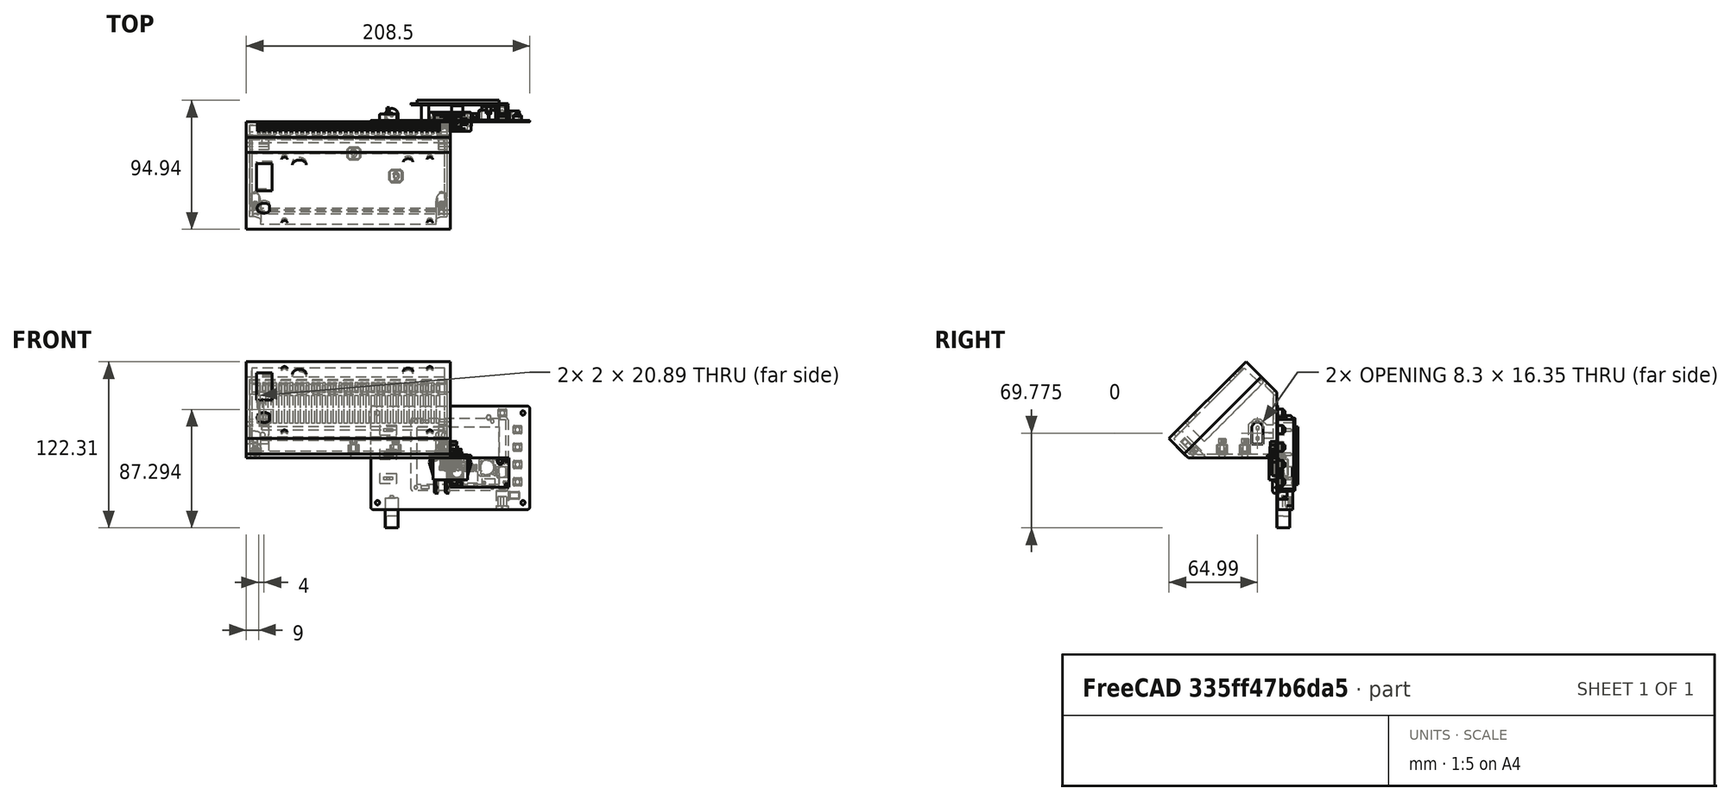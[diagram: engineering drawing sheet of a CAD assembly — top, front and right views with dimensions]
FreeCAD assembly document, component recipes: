
FREECAD ASSEMBLY — COMPONENT RECIPES ("oscillo_010_surBase35mm_007.5")

This assembly document has 19 components, labeled P0..P18 below (a component is one placed body or linked part). 12 of them carry a construction recipe — the FreeCAD feature program that regenerates the part from scratch, quoted from this document or its linked companion documents; the rest are supplied as boundary geometry only. No exploded tour is included for this assembly.
COMPONENT P0 — recipe-attached ("base", modeled in this document).
Construction recipe (the document's own serialized feature program — sketch geometry with constraints, then the solid features built on it; lengths are millimeters unless a unit is written):

FEATURE [PartDesign::FeatureBase] Clone
  BaseFeature = -> Slice_child0
FEATURE [PartDesign::Thickness] Thickness
  Base = -> Clone [Face7]
  BaseFeature = -> Clone
  Intersection = false
  Join = 0
  Mode = 0
  Reversed = true
  SupportTransform = false
  Value = 2.5
  expr: Value = <<sp>>.epaisseurParois
FEATURE [PartDesign::Plane] DatumPlane001  label="planXt"
  AttachmentOffset = pos=(0,0,-2.5) rot=(0,0,1;0rad)
  Length = 110.737
  MapMode = 5
  Placement = pos=(-2.5,6e-16,-6e-16) rot=(0.57735,0.57735,0.57735;2.0944rad)
  ResizeMode = 0
  Support = -> [YZ_Plane002]
  Width = 102.305
  expr: .AttachmentOffset.Base.z = -<<sp>>.epaisseurParois
FEATURE [Sketcher::SketchObject] Sketch002  label="sk_renfortXt"
  FullyConstrained = true
  MapMode = 5
  Placement = pos=(-2.5,6e-16,-6e-16) rot=(0.57735,0.57735,0.57735;2.0944rad)
  Support = -> [DatumPlane001]
  expr: .Constraints.dist = <<sp>>.xt60distanceAngleBord
  expr: .Constraints.epRf = <<sp>>.xt60epRenfort
  expr: Constraints[13] = <<sp>>.xt60largeurFetiere
  expr: Constraints[14] = <<sp>>.xt60hauteur
  expr: Constraints[15] = <<sp>>.xt60hauteurToit
  expr: Constraints[16] = <<sp>>.xt60base
  expr: Constraints[18] = .Constraints.dist
  expr: Constraints[31] = <<sp>>.epaisseurParois
  expr: Constraints[32] = .Constraints.epRf
  expr: Constraints[34] = .Constraints.epRf
  expr: Constraints[45] = <<sp>>.epaisseurParois
  sketch-geometry (17):
    g0: LineSegment StartX=-18.3 StartY=10 StartZ=0 EndX=-18.3 EndY=23.25 EndZ=0
    g1: LineSegment StartX=-18.3 StartY=23.25 StartZ=0 EndX=-15.65 EndY=25.75 EndZ=0
    g2: LineSegment StartX=-15.65 StartY=25.75 StartZ=0 EndX=-12.65 EndY=25.75 EndZ=0
    g3: LineSegment StartX=-12.65 StartY=25.75 StartZ=0 EndX=-10 EndY=23.25 EndZ=0
    g4: LineSegment StartX=-10 StartY=23.25 StartZ=0 EndX=-10 EndY=10 EndZ=0
    g5: LineSegment StartX=-10 StartY=10 StartZ=0 EndX=-18.3 EndY=10 EndZ=0
    g6: LineSegment StartX=-14.15 StartY=10 StartZ=0 EndX=-14.15 EndY=25.75 EndZ=0
    g7: LineSegment StartX=-16.6431 StartY=28.25 StartZ=0 EndX=-20.8 EndY=24.3284 EndZ=0
    g8: LineSegment StartX=-20.8 StartY=24.3284 StartZ=0 EndX=-20.8 EndY=2.5 EndZ=0
    g9: LineSegment StartX=-20.8 StartY=2.5 StartZ=0 EndX=-7.5 EndY=2.5 EndZ=0
    g10: LineSegment StartX=-7.5 StartY=2.5 StartZ=0 EndX=-7.5 EndY=24.3284 EndZ=0
    g11: LineSegment StartX=-7.5 StartY=24.3284 StartZ=0 EndX=-11.6569 EndY=28.25 EndZ=0
    g12: LineSegment StartX=-11.6569 StartY=28.25 StartZ=0 EndX=-16.6431 EndY=28.25 EndZ=0
    g13: LineSegment StartX=-7.5 StartY=24.3284 StartZ=0 EndX=-2.5 EndY=24.3284 EndZ=0
    g14: LineSegment StartX=-2.5 StartY=24.3284 StartZ=0 EndX=-2.5 EndY=2.5 EndZ=0
    g15: LineSegment StartX=-2.5 StartY=2.5 StartZ=0 EndX=-7.5 EndY=2.5 EndZ=0
    g16: LineSegment StartX=-7.5 StartY=2.5 StartZ=0 EndX=-7.5 EndY=24.3284 EndZ=0
  constraints (46):
    c: Vertical(g0)
    c: Coincident(g0,g1)
    c: Coincident(g1,g2)
    c: Horizontal(g2)
    c: Coincident(g2,g3)
    c: Coincident(g3,g4)
    c: Vertical(g4)
    c: Coincident(g4,g5)
    c: Coincident(g5,g0)
    c: Horizontal(g5)
    c: Symmetric(g1,g2,g6)
    c: Equal(g0,g4)
    c: Symmetric(g0,g4,g6)
    c: DistanceX(g2,g2) = 3
    c: DistanceY(g4,g4) = 13.25
    c: DistanceY(g3,g2) = 2.5
    c: DistanceX(g5,g5) = 8.3
    c: DistanceX(g4,g-1) = 10  'dist'
    c: DistanceY(g-1,g4) = 10
    c: Coincident(g7,g8)
    c: Vertical(g8)
    c: Coincident(g8,g9)
    c: Horizontal(g9)
    c: Coincident(g9,g10)
    c: Coincident(g10,g11)
    c: Coincident(g11,g12)
    c: Coincident(g12,g7)
    c: Symmetric(g7,g10,g6)
    c: Symmetric(g7,g11,g6)
    c: Symmetric(g8,g9,g6)
    c: DistanceX(g8,g0) = 2.5  'epRf'
    c: DistanceY(g-1,g9) = 2.5
    c: Distance(g7,g1) = 2.5
    c: Parallel(g1,g7)
    c: DistanceY(g2,g11) = 2.5
    c: Coincident(g13,g14)
    c: Coincident(g14,g15)
    c: Coincident(g15,g16)
    c: Coincident(g16,g13)
    c: Horizontal(g13)
    c: Horizontal(g15)
    c: Vertical(g14)
    c: Vertical(g16)
    c: Coincident(g13,g11)
    c: Horizontal(g14,g9)
    c: DistanceX(g14,g-1) = 2.5
FEATURE [PartDesign::Pad] Pad001  label="renfortXt"
  AllowMultiFace = false
  BaseFeature = -> Thickness
  Direction = (1,1,1)
  Length = 145
  Length2 = 100
  Profile = -> Sketch002
  Reversed = true
  Type = 0
  expr: Length = <<sp>>.largeurModuleBase - 2 * <<sp>>.epaisseurParois
FEATURE [Sketcher::SketchObject] Sketch003  label="sk_trouXt"
  FullyConstrained = true
  MapMode = 5
  Placement = pos=(0,0,0) rot=(0.57735,0.57735,0.57735;2.0944rad)
  Support = -> [YZ_Plane002]
  expr: .Constraints.dist = <<sp>>.xt60distanceAngleBord
  expr: Constraints[13] = <<sp>>.xt60base
  expr: Constraints[14] = <<sp>>.xt60hauteur
  expr: Constraints[15] = <<sp>>.xt60hauteurToit + <<sp>>.xtJeu
  expr: Constraints[16] = <<sp>>.xt60largeurFetiere
  expr: Constraints[18] = .Constraints.dist
  sketch-geometry (7):
    g0: LineSegment StartX=-18.3 StartY=10 StartZ=0 EndX=-18.3 EndY=23.25 EndZ=0
    g1: LineSegment StartX=-18.3 StartY=23.25 StartZ=0 EndX=-15.65 EndY=26.35 EndZ=0
    g2: LineSegment StartX=-15.65 StartY=26.35 StartZ=0 EndX=-12.65 EndY=26.35 EndZ=0
    g3: LineSegment StartX=-12.65 StartY=26.35 StartZ=0 EndX=-10 EndY=23.25 EndZ=0
    g4: LineSegment StartX=-10 StartY=23.25 StartZ=0 EndX=-10 EndY=10 EndZ=0
    g5: LineSegment StartX=-10 StartY=10 StartZ=0 EndX=-18.3 EndY=10 EndZ=0
    g6: LineSegment StartX=-14.15 StartY=10 StartZ=0 EndX=-14.15 EndY=26.35 EndZ=0
  constraints (19):
    c: Vertical(g0)
    c: Coincident(g0,g1)
    c: Coincident(g1,g2)
    c: Horizontal(g2)
    c: Coincident(g2,g3)
    c: Coincident(g3,g4)
    c: Coincident(g4,g5)
    c: Coincident(g5,g0)
    c: Horizontal(g5)
    c: Symmetric(g1,g2,g6)
    c: Symmetric(g0,g3,g6)
    c: Vertical(g6)
    c: Symmetric(g0,g4,g6)
    c: DistanceX(g5,g5) = 8.3
    c: DistanceY(g4,g4) = 13.25
    c: DistanceY(g3,g2) = 3.1
    c: DistanceX(g2,g2) = 3
    c: DistanceX(g4,g-1) = 10  'dist'
    c: DistanceY(g-1,g4) = 10
FEATURE [PartDesign::Pocket] Pocket
  AllowMultiFace = false
  BaseFeature = -> Pad001
  Direction = (1,1,1)
  Length = 150
  Length2 = 100
  Profile = -> Sketch003
  Type = 0
  expr: Length = <<sp>>.largeurModuleBase
FEATURE [PartDesign::Plane] DatumPlane002  label="planDecoupeRenfortXt"
  AttachmentOffset = pos=(0,0,2.5) rot=(0,0,1;0rad)
  Length = 199.331
  MapMode = 5
  Placement = pos=(0,-2.5,-6e-16) rot=(1,0,0;1.5708rad)
  ResizeMode = 0
  Support = -> [XZ_Plane002]
  Width = 108.899
  expr: .AttachmentOffset.Base.z = <<sp>>.epaisseurParois
FEATURE [Sketcher::SketchObject] Sketch004  label="sk_decoupRenfXt"
  FullyConstrained = true
  MapMode = 5
  Placement = pos=(0,-2.5,-6e-16) rot=(1,0,0;1.5708rad)
  Support = -> [DatumPlane002]
  expr: Constraints[10] = <<sp>>.xt60LongueurRenfortPetit + <<sp>>.epaisseurParois
  expr: Constraints[11] = <<sp>>.largeurModuleBase - (<<sp>>.xt60longueurRenfortGrand + <<sp>>.epaisseurParois)
  expr: Constraints[8] = <<sp>>.epaisseurParois
  expr: Constraints[9] = <<sp>>.xt60distanceAngleBord + <<sp>>.xt60hauteur + <<sp>>.xt60hauteurToit + <<sp>>.xt60epRenfort
  sketch-geometry (4):
    g0: LineSegment StartX=-133.5 StartY=28.25 StartZ=0 EndX=-8.5 EndY=28.25 EndZ=0
    g1: LineSegment StartX=-8.5 StartY=28.25 StartZ=0 EndX=-8.5 EndY=2.5 EndZ=0
    g2: LineSegment StartX=-8.5 StartY=2.5 StartZ=0 EndX=-133.5 EndY=2.5 EndZ=0
    g3: LineSegment StartX=-133.5 StartY=2.5 StartZ=0 EndX=-133.5 EndY=28.25 EndZ=0
  constraints (12):
    c: Coincident(g0,g1)
    c: Coincident(g1,g2)
    c: Coincident(g2,g3)
    c: Coincident(g3,g0)
    c: Horizontal(g0)
    c: Horizontal(g2)
    c: Vertical(g1)
    c: Vertical(g3)
    c: DistanceY(g-1,g1) = 2.5
    c: DistanceY(g-1,g0) = 28.25
    c: DistanceX(g1,g-1) = 8.5
    c: DistanceX(g2,g-1) = 133.5
FEATURE [PartDesign::Pocket] Pocket001  label="decoupeRenfXt"
  AllowMultiFace = false
  BaseFeature = -> Pocket
  Direction = (1,1,1)
  Length = 23.3
  Length2 = 100
  Profile = -> Sketch004
  Reversed = true
  Type = 0
  expr: Length = <<sp>>.xt60distanceAngleBord + <<sp>>.xt60base + 2 * <<sp>>.xt60epRenfort
FEATURE [Sketcher::SketchObject] Sketch005  label="xt60PercagePostMale"
  FullyConstrained = true
  MapMode = 5
  Placement = pos=(0,0,0) rot=(1,0,0;1.5708rad)
  Support = -> [XZ_Plane002]
  expr: Constraints[0] = <<sp>>.insertDiamPercage
  expr: Constraints[1] = <<sp>>.insertDistanceTrouBordMale
  expr: Constraints[2] = <<sp>>.insertHauteur
  sketch-geometry (1):
    g0: Circle CenterX=-4.5 CenterY=16.625 CenterZ=0 NormalX=0 NormalY=0 NormalZ=1 AngleXU=0 Radius=2
  constraints (3):
    c: Diameter(g0) = 4
    c: DistanceX(g0,g-1) = 4.5
    c: DistanceY(g-1,g0) = 16.625
FEATURE [PartDesign::Pocket] Pocket002  label="insertXtMale"
  AllowMultiFace = false
  BaseFeature = -> Pocket001
  Direction = (1,1,1)
  Length = 10
  Length2 = 100
  Profile = -> Sketch005
  Reversed = true
  Type = 0
  expr: Length = <<sp>>.insertProfondeurPercage
FEATURE [Sketcher::SketchObject] Sketch006  label="xt60PercagePostFem"
  FullyConstrained = true
  MapMode = 5
  Placement = pos=(0,0,0) rot=(1,0,0;1.5708rad)
  Support = -> [XZ_Plane002]
  expr: Constraints[0] = <<sp>>.insertDiamPercage
  expr: Constraints[1] = <<sp>>.insertDistanceTrouBordFem
  expr: Constraints[2] = <<sp>>.insertHauteur
  sketch-geometry (1):
    g0: Circle CenterX=-138 CenterY=16.625 CenterZ=0 NormalX=0 NormalY=0 NormalZ=1 AngleXU=0 Radius=2
  constraints (3):
    c: Diameter(g0) = 4
    c: DistanceX(g0,g-1) = 138
    c: DistanceY(g-1,g0) = 16.625
FEATURE [PartDesign::Pocket] Pocket003  label="insertXt60Fem"
  AllowMultiFace = false
  BaseFeature = -> Pocket002
  Direction = (1,1,1)
  Length = 10
  Length2 = 100
  Profile = -> Sketch006
  Reversed = true
  Type = 0
  expr: Length = <<sp>>.insertProfondeurPercage
FEATURE [PartDesign::Plane] DatumPlane003
  AttachmentOffset = pos=(0,0,2.5) rot=(0,0,1;0rad)
  Length = 200.515
  MapMode = 2
  Placement = pos=(0,0,2.5) rot=(0,0,1;0rad)
  ResizeMode = 0
  Support = -> [XY_Plane002]
  Width = 118.515
  expr: .AttachmentOffset.Base.z = <<sp>>.epaisseurParois
FEATURE [PartDesign::Plane] DatumPlane004  label="planTrancheur"
  AttachmentOffset = pos=(0,0,71) rot=(-1,0,0;0.785398rad)
  Length = 204.647
  MapMode = 5
  Placement = pos=(0,-71,-1.58e-14) rot=(1,0,0;0.785398rad)
  ResizeMode = 0
  Support = -> [XZ_Plane002]
  Width = 155.206
  expr: .AttachmentOffset.Base.z = <<sp>>.planTrancheur
FEATURE [Sketcher::SketchObject] Sketch008
  FullyConstrained = true
  MapMode = 5
  Placement = pos=(0,-71,-2.13e-14) rot=(1,0,0;0.785398rad)
  Support = -> [DatumPlane004]
  expr: .Constraints.dist = <<sp>>.epaisseurParois
  expr: Constraints[13] = <<sp>>.epaisseurParois
  expr: Constraints[16] = <<sp>>.insertDiamPercage / 2 + <<sp>>.insertFAVMargeDist
  expr: Constraints[1] = <<sp>>.insertFavDistAuZeroDuPLan
  expr: Constraints[21] = <<sp>>.insertFAVDistBord
  expr: Constraints[22] = <<sp>>.largeurModuleBase - <<sp>>.epaisseurParois
  sketch-geometry (7):
    g0: LineSegment StartX=-2.5 StartY=4.24264 StartZ=0 EndX=-147.5 EndY=4.24264 EndZ=0
    g1: LineSegment StartX=-6.5 StartY=14.7426 StartZ=0 EndX=-2.5 EndY=14.7426 EndZ=0
    g2: LineSegment StartX=-2.5 StartY=14.7426 StartZ=0 EndX=-2.5 EndY=6.74264 EndZ=0
    g3: LineSegment StartX=-2.5 StartY=6.74264 StartZ=0 EndX=-10.5 EndY=6.74264 EndZ=0
    g4: LineSegment StartX=-10.5 StartY=6.74264 StartZ=0 EndX=-10.5 EndY=10.7426 EndZ=0
    g5: ArcOfCircle CenterX=-6.5 CenterY=10.7426 CenterZ=0 NormalX=0 NormalY=0 NormalZ=1 AngleXU=0 Radius=4 StartAngle=1.5708 EndAngle=3.14159
    g6: LineSegment StartX=-6.5 StartY=10.7426 StartZ=0 EndX=-6.5 EndY=6.74264 EndZ=0
  constraints (23):
    c: Horizontal(g0)
    c: DistanceY(g-1,g0) = 4.24264
    c: DistanceX(g0,g-1) = 2.5  'dist'
    c: Horizontal(g1)
    c: Coincident(g1,g2)
    c: Vertical(g2)
    c: Coincident(g2,g3)
    c: Horizontal(g3)
    c: Coincident(g3,g4)
    c: Vertical(g4)
    c: Vertical(g2,g0)
    c: Equal(g3,g2)
    c: Equal(g4,g1)
    c: DistanceY(g0,g2) = 2.5
    c: Coincident(g5,g4)
    c: Coincident(g5,g1)
    c: DistanceX(g5,g2) = 4
    c: Coincident(g6,g5)
    c: PointOnObject(g6,g3)
    c: Vertical(g6)
    c: Vertical(g5,g1)
    c: DistanceX(g3,g3) = 8
    c: DistanceX(g0,g-1) = 147.5
FEATURE [PartDesign::Pad] Pad003  label="padTrouFAVDroite"
  AllowMultiFace = false
  BaseFeature = -> Pocket003
  Direction = (1,1,1)
  Length = 10
  Length2 = 100
  Profile = -> Sketch008
  Reversed = true
  Type = 3
  UpToFace = -> DatumPlane003
FEATURE [Sketcher::SketchObject] Sketch009
  FullyConstrained = true
  MapMode = 5
  Placement = pos=(0,-71,-2.13e-14) rot=(1,0,0;0.785398rad)
  Support = -> [DatumPlane004]
  expr: .Constraints.larg = <<sp>>.insertFAVDistBord
  expr: Constraints[11] = .Constraints.larg / 2
  expr: Constraints[12] = <<sp>>.largeurModuleBase
  expr: Constraints[13] = <<sp>>.insertFavDistAuZeroDuPLan
  expr: Constraints[14] = <<sp>>.epaisseurParois
  expr: Constraints[15] = <<sp>>.epaisseurParois
  expr: Constraints[8] = .Constraints.larg
  sketch-geometry (6):
    g0: LineSegment StartX=-147.5 StartY=6.74264 StartZ=0 EndX=-139.5 EndY=6.74264 EndZ=0
    g1: LineSegment StartX=-139.5 StartY=6.74264 StartZ=0 EndX=-139.5 EndY=10.7426 EndZ=0
    g2: LineSegment StartX=-143.5 StartY=14.7426 StartZ=0 EndX=-147.5 EndY=14.7426 EndZ=0
    g3: LineSegment StartX=-147.5 StartY=14.7426 StartZ=0 EndX=-147.5 EndY=6.74264 EndZ=0
    g4: ArcOfCircle CenterX=-143.5 CenterY=10.7426 CenterZ=0 NormalX=0 NormalY=0 NormalZ=1 AngleXU=0 Radius=4 StartAngle=0 EndAngle=1.5708
    g5: GeomPoint X=-150 Y=4.24264 Z=0
  constraints (16):
    c: Coincident(g0,g1)
    c: Coincident(g2,g3)
    c: Coincident(g3,g0)
    c: Horizontal(g0)
    c: Horizontal(g2)
    c: Vertical(g1)
    c: Vertical(g3)
    c: DistanceX(g0,g0) = 8  'larg'
    c: DistanceY(g3,g3) = 8
    c: Tangent(g2,g4) = -1.5708
    c: Tangent(g1,g4) = -1.5708
    c: DistanceX(g0,g4) = 4
    c: DistanceX(g5,g-1) = 150
    c: DistanceY(g-1,g5) = 4.24264
    c: DistanceX(g5,g0) = 2.5
    c: DistanceY(g5,g0) = 2.5
FEATURE [PartDesign::Pad] Pad004  label="padTrouFavGauche"
  AllowMultiFace = false
  BaseFeature = -> Pad003
  Direction = (1,1,1)
  Length = 10
  Length2 = 100
  Profile = -> Sketch009
  Type = 3
  UpToFace = -> DatumPlane003 [Plane]
FEATURE [Sketcher::SketchObject] Sketch010
  FullyConstrained = true
  MapMode = 5
  Placement = pos=(0,-71,-2.13e-14) rot=(1,0,0;0.785398rad)
  Support = -> [DatumPlane004]
  expr: Constraints[0] = <<sp>>.insertFAVDistBord / 2 + <<sp>>.epaisseurParois
  expr: Constraints[1] = <<sp>>.insertFavDistAuZeroDuPLan + <<sp>>.epaisseurParois + <<sp>>.insertFAVDistBord / 2
  expr: Constraints[2] = <<sp>>.insertDiamPercage
  sketch-geometry (1):
    g0: Circle CenterX=-6.5 CenterY=10.7426 CenterZ=0 NormalX=0 NormalY=0 NormalZ=1 AngleXU=0 Radius=2
  constraints (3):
    c: DistanceX(g0,g-1) = 6.5
    c: DistanceY(g-1,g0) = 10.7426
    c: Diameter(g0) = 4
FEATURE [PartDesign::Pocket] Pocket004  label="trouDroit"
  AllowMultiFace = false
  BaseFeature = -> Pad004
  Direction = (1,1,1)
  Length = 5
  Length2 = 100
  Profile = -> Sketch010
  Type = 1
FEATURE [Sketcher::SketchObject] Sketch011
  FullyConstrained = true
  MapMode = 5
  Placement = pos=(0,-71,-2.13e-14) rot=(1,0,0;0.785398rad)
  Support = -> [DatumPlane004]
  expr: Constraints[0] = <<sp>>.insertDiamPercage
  expr: Constraints[1] = <<sp>>.largeurModuleBase - <<sp>>.epaisseurParois - <<sp>>.insertFAVDistBord / 2
  expr: Constraints[2] = <<sp>>.insertFavDistAuZeroDuPLan + <<sp>>.epaisseurParois + <<sp>>.insertFAVDistBord / 2
  sketch-geometry (1):
    g0: Circle CenterX=-143.5 CenterY=10.7426 CenterZ=0 NormalX=0 NormalY=0 NormalZ=1 AngleXU=0 Radius=2
  constraints (3):
    c: Diameter(g0) = 4
    c: DistanceX(g0,g-1) = 143.5
    c: DistanceY(g-1,g0) = 10.7426
FEATURE [PartDesign::Pocket] Pocket005  label="trouGauche"
  AllowMultiFace = false
  BaseFeature = -> Pocket004
  Direction = (1,1,1)
  Length = 5
  Length2 = 100
  Profile = -> Sketch011
  Type = 1
FEATURE [PartDesign::Plane] DatumPlane005  label="planTeteVisFav"
  AttachmentOffset = pos=(0,0,68) rot=(-1,0,0;0.785398rad)
  Length = 204.647
  MapMode = 5
  Placement = pos=(0,-68,-1.51e-14) rot=(1,0,0;0.785398rad)
  ResizeMode = 0
  Support = -> [XZ_Plane002]
  Width = 155.206
  expr: .AttachmentOffset.Base.z = <<sp>>.planTrancheur - 3
FEATURE [Sketcher::SketchObject] Sketch012
  ExternalGeometry = -> [Pocket005]
  FullyConstrained = true
  MapMode = 5
  Placement = pos=(0,-68,-1.42e-14) rot=(1,0,0;0.785398rad)
  Support = -> [DatumPlane005]
  expr: Constraints[1] = <<sp>>.visM3DiamEncastrement
  sketch-geometry (2):
    g0: Circle CenterX=-6.5 CenterY=8.62132 CenterZ=0 NormalX=0 NormalY=0 NormalZ=1 AngleXU=0 Radius=3
    g1: Circle CenterX=-143.5 CenterY=8.62132 CenterZ=0 NormalX=0 NormalY=0 NormalZ=1 AngleXU=0 Radius=3
  constraints (4):
    c: Equal(g0,g1)
    c: Diameter(g1) = 6
    c: Coincident(g1,g-4)
    c: Coincident(g-3,g0)
FEATURE [PartDesign::Pocket] Pocket006  label="evidementTeteVisFav"
  AllowMultiFace = false
  BaseFeature = -> Pocket005
  Direction = (1,1,1)
  Length = 20
  Length2 = 100
  Profile = -> Sketch012
  Type = 1
FEATURE [Sketcher::SketchObject] Sketch014
  FullyConstrained = true
  MapMode = 5
  Placement = pos=(0,0,0) rot=(1,0,0;1.5708rad)
  Support = -> [XZ_Plane002]
  expr: Constraints[12] = <<sp>>.xt60distanceAngleBord + <<sp>>.xt60hauteur + <<sp>>.ventilDistBordFente
  expr: Constraints[13] = <<sp>>.ventilLargeurFentes
  expr: Constraints[14] = <<sp>>.ventilEcartfente / 2
  expr: Constraints[15] = <<sp>>.hauteurDuDos - <<sp>>.ventilDistBordFente
  expr: Constraints[2] = <<sp>>.hauteurDuDos
  expr: Constraints[3] = <<sp>>.largeurModuleBase / 2
  sketch-geometry (5):
    g0: LineSegment StartX=-75 StartY=0 StartZ=0 EndX=-75 EndY=48.1371 EndZ=0
    g1: LineSegment StartX=-78 StartY=46.1371 StartZ=0 EndX=-76 EndY=46.1371 EndZ=0
    g2: LineSegment StartX=-76 StartY=46.1371 StartZ=0 EndX=-76 EndY=25.25 EndZ=0
    g3: LineSegment StartX=-76 StartY=25.25 StartZ=0 EndX=-78 EndY=25.25 EndZ=0
    g4: LineSegment StartX=-78 StartY=25.25 StartZ=0 EndX=-78 EndY=46.1371 EndZ=0
  constraints (16):
    c: PointOnObject(g0,g-1)
    c: Vertical(g0)
    c: DistanceY(g0,g0) = 48.1371
    c: DistanceX(g0,g-1) = 75
    c: Coincident(g1,g2)
    c: Coincident(g2,g3)
    c: Coincident(g3,g4)
    c: Coincident(g4,g1)
    c: Horizontal(g1)
    c: Horizontal(g3)
    c: Vertical(g2)
    c: Vertical(g4)
    c: DistanceY(g-1,g2) = 25.25
    c: DistanceX(g1,g1) = 2
    c: DistanceX(g2,g0) = 1
    c: DistanceY(g-1,g1) = 46.1371
FEATURE [PartDesign::Pocket] Pocket008  label="ventilFente1"
  AllowMultiFace = false
  BaseFeature = -> Pocket006
  Direction = (1,1,1)
  Length = 2.5
  Length2 = 100
  Profile = -> Sketch014
  Reversed = true
  Type = 0
  expr: Length = <<sp>>.epaisseurParois
FEATURE [PartDesign::LinearPattern] LinearPattern  label="ventilDosRepeat1"
  BaseFeature = -> Pocket008
  Direction = -> Sketch014 [H_Axis]
  Length = 64
  Occurrences = 17
  Originals = -> [Pocket008]
  Reversed = true
  expr: Length = <<sp>>.ventilLargeurRepet
  expr: Occurrences = <<sp>>.ventilNbrFents
FEATURE [PartDesign::LinearPattern] LinearPattern001  label="ventilDosRepeat2"
  BaseFeature = -> LinearPattern
  Direction = -> Sketch014 [H_Axis]
  Length = 68
  Occurrences = 18
  Originals = -> [Pocket008]
  expr: Length = <<sp>>.ventilLargeurRepet + <<sp>>.ventilEcartfente + <<sp>>.ventilLargeurFentes
  expr: Occurrences = <<sp>>.ventilNbrFents + 1
FEATURE [PartDesign::Plane] DatumPlane006  label="planVentilSup"
  AttachmentOffset = pos=(0,0,-48.1371) rot=(1,0,0;0.785398rad)
  Length = 204.647
  MapMode = 5
  Placement = pos=(0,48.1371,1.07e-14) rot=(1,0,0;2.35619rad)
  ResizeMode = 0
  Support = -> [XZ_Plane002]
  Width = 155.206
  expr: .AttachmentOffset.Base.z = -<<sp>>.hauteurDuDos
FEATURE [Sketcher::SketchObject] Sketch015
  FullyConstrained = true
  MapMode = 5
  Placement = pos=(0,48.1371,1.07e-14) rot=(1,0,0;2.35619rad)
  Support = -> [DatumPlane006]
  expr: Constraints[10] = <<sp>>.ventilLargeurFentes
  expr: Constraints[11] = (<<sp>>.largeurModuleBase + <<sp>>.ventilEcartfente) / 2
  expr: Constraints[8] = <<sp>>.distanceAuZeroPlanBorArriere + <<sp>>.ventilDistBordFente
  expr: Constraints[9] = <<sp>>.longPetitRetSupSansFav - 2 * <<sp>>.ventilDistBordFente - <<sp>>.favBordureProf
  sketch-geometry (4):
    g0: LineSegment StartX=-76 StartY=78.0926 StartZ=0 EndX=-78 EndY=78.0926 EndZ=0
    g1: LineSegment StartX=-78 StartY=78.0926 StartZ=0 EndX=-78 EndY=70.0761 EndZ=0
    g2: LineSegment StartX=-78 StartY=70.0761 StartZ=0 EndX=-76 EndY=70.0761 EndZ=0
    g3: LineSegment StartX=-76 StartY=70.0761 StartZ=0 EndX=-76 EndY=78.0926 EndZ=0
  constraints (12):
    c: Coincident(g0,g1)
    c: Coincident(g1,g2)
    c: Coincident(g2,g3)
    c: Coincident(g3,g0)
    c: Horizontal(g0)
    c: Horizontal(g2)
    c: Vertical(g1)
    c: Vertical(g3)
    c: DistanceY(g-1,g2) = 70.0761
    c: DistanceY(g2,g0) = 8.01652
    c: DistanceX(g0,g0) = 2
    c: DistanceX(g2,g-1) = 76
FEATURE [PartDesign::Pocket] Pocket009  label="ventilSupFente"
  AllowMultiFace = false
  BaseFeature = -> LinearPattern001
  Direction = (1,1,1)
  Length = 5
  Length2 = 100
  Profile = -> Sketch015
  Reversed = true
  Type = 0
FEATURE [PartDesign::LinearPattern] LinearPattern002  label="ventilSupRepeat1"
  BaseFeature = -> Pocket009
  Direction = -> Sketch015 [H_Axis]
  Length = 64
  Occurrences = 17
  Originals = -> [Pocket009]
  Reversed = true
  expr: Length = <<sp>>.ventilLargeurRepet
  expr: Occurrences = <<sp>>.ventilNbrFents
FEATURE [PartDesign::LinearPattern] LinearPattern003  label="ventilSupRepeat2"
  BaseFeature = -> LinearPattern002
  Direction = -> Sketch015 [H_Axis]
  Length = 68
  Occurrences = 18
  Originals = -> [Pocket009]
  expr: Length = <<sp>>.ventilLargeurRepet + <<sp>>.ventilEcartfente + <<sp>>.ventilLargeurFentes
  expr: Occurrences = <<sp>>.ventilNbrFents + 1
FEATURE [PartDesign::Body] Body001  label="base"
  BaseFeature = -> Slice_child0
  Group = -> [Clone,Thickness,DatumPlane001,Sketch002,Pad001,Sketch003,Pocket,DatumPlane002,Sketch004,Pocket001,Sketch005,Pocket002,Sketch006,Pocket003,DatumPlane003,DatumPlane004,Sketch008,Pad003,Sketch009,Pad004,Sketch010,Pocket004,Sketch011,Pocket005,DatumPlane005,Sketch012,Pocket006,Sketch014,Pocket008,LinearPattern,LinearPattern001,DatumPlane006,Sketch015,Pocket009,LinearPattern002,LinearPattern003,+10 more]
  Origin = -> Origin002
  Tip = -> Chamfer005
COMPONENT P1 — recipe-attached ("faceAvant", modeled in this document).
Construction recipe (the document's own serialized feature program — sketch geometry with constraints, then the solid features built on it; lengths are millimeters unless a unit is written):

FEATURE [PartDesign::FeatureBase] Clone001
  BaseFeature = -> Slice_child1
FEATURE [PartDesign::Thickness] Thickness001
  Base = -> Clone001 [Face5]
  BaseFeature = -> Clone001
  Intersection = false
  Join = 0
  Mode = 0
  Reversed = true
  SupportTransform = false
  Value = 2.5
  expr: Value = <<sp>>.epaisseurParois
FEATURE [PartDesign::Plane] DatumPlane007  label="planTrancheurBis"
  AttachmentOffset = pos=(0,0,71) rot=(-1,0,0;0.785398rad)
  Length = 206.452
  MapMode = 5
  Placement = pos=(0,-71,-1.58e-14) rot=(1,0,0;0.785398rad)
  ResizeMode = 0
  Support = -> [XZ_Plane003]
  Width = 172.769
  expr: .AttachmentOffset.Base.z = <<sp>>.planTrancheur
FEATURE [Sketcher::SketchObject] Sketch016  label="sk_insertFavDroit"
  FullyConstrained = true
  MapMode = 5
  Placement = pos=(0,-71,-2.13e-14) rot=(1,0,0;0.785398rad)
  Support = -> [DatumPlane007]
  expr: Constraints[11] = <<sp>>.insertFAVDistBord
  expr: Constraints[14] = <<sp>>.insertFAVDistBord / 2
  expr: Constraints[7] = <<sp>>.epaisseurParois
  expr: Constraints[8] = <<sp>>.insertFavDistAuZeroDuPLan + <<sp>>.epaisseurParois
  expr: Constraints[9] = <<sp>>.insertFAVDistBord
  sketch-geometry (5):
    g0: LineSegment StartX=-6.5 StartY=14.7426 StartZ=0 EndX=-2.5 EndY=14.7426 EndZ=0
    g1: LineSegment StartX=-2.5 StartY=14.7426 StartZ=0 EndX=-2.5 EndY=6.74264 EndZ=0
    g2: LineSegment StartX=-2.5 StartY=6.74264 StartZ=0 EndX=-10.5 EndY=6.74264 EndZ=0
    g3: LineSegment StartX=-10.5 StartY=6.74264 StartZ=0 EndX=-10.5 EndY=10.7426 EndZ=0
    g4: ArcOfCircle CenterX=-6.5 CenterY=10.7426 CenterZ=0 NormalX=0 NormalY=0 NormalZ=1 AngleXU=0 Radius=4 StartAngle=1.5708 EndAngle=3.14159
  constraints (15):
    c: Horizontal(g0)
    c: Coincident(g0,g1)
    c: Vertical(g1)
    c: Coincident(g1,g2)
    c: Horizontal(g2)
    c: Coincident(g2,g3)
    c: Vertical(g3)
    c: DistanceX(g1,g-1) = 2.5
    c: DistanceY(g-1,g1) = 6.74264
    c: DistanceY(g1,g1) = 8
    c: Equal(g3,g0)
    c: DistanceX(g2,g2) = 8
    c: Coincident(g4,g0)
    c: Tangent(g4,g3) = 1.5708
    c: DistanceX(g4,g1) = 4
FEATURE [PartDesign::Pad] Pad005  label="padInsertFavDroit"
  AllowMultiFace = false
  BaseFeature = -> Thickness001
  Direction = (1,1,1)
  Length = 10
  Length2 = 100
  Profile = -> Sketch016
  Type = 2
FEATURE [Sketcher::SketchObject] Sketch017  label="sp_padInserFavGauch"
  FullyConstrained = true
  MapMode = 5
  Placement = pos=(0,-71,-2.13e-14) rot=(1,0,0;0.785398rad)
  Support = -> [DatumPlane007]
  expr: Constraints[10] = <<sp>>.insertFAVDistBord
  expr: Constraints[12] = <<sp>>.insertFAVDistBord / 2
  expr: Constraints[13] = <<sp>>.largeurModuleBase
  expr: Constraints[14] = <<sp>>.insertFavDistAuZeroDuPLan
  expr: Constraints[15] = <<sp>>.epaisseurParois
  expr: Constraints[16] = <<sp>>.epaisseurParois
  sketch-geometry (6):
    g0: LineSegment StartX=-143.5 StartY=14.7426 StartZ=0 EndX=-147.5 EndY=14.7426 EndZ=0
    g1: LineSegment StartX=-147.5 StartY=14.7426 StartZ=0 EndX=-147.5 EndY=6.74264 EndZ=0
    g2: LineSegment StartX=-147.5 StartY=6.74264 StartZ=0 EndX=-139.5 EndY=6.74264 EndZ=0
    g3: LineSegment StartX=-139.5 StartY=6.74264 StartZ=0 EndX=-139.5 EndY=10.7426 EndZ=0
    g4: ArcOfCircle CenterX=-143.5 CenterY=10.7426 CenterZ=0 NormalX=0 NormalY=0 NormalZ=1 AngleXU=0 Radius=4 StartAngle=0 EndAngle=1.5708
    g5: GeomPoint X=-150 Y=4.24264 Z=0
  constraints (17):
    c: Horizontal(g0)
    c: Coincident(g0,g1)
    c: Vertical(g1)
    c: Coincident(g1,g2)
    c: Horizontal(g2)
    c: Coincident(g2,g3)
    c: Vertical(g3)
    c: Equal(g3,g0)
    c: Equal(g2,g1)
    c: Coincident(g0,g4)
    c: DistanceX(g2,g2) = 8
    c: Tangent(g4,g3) = -1.5708
    c: DistanceX(g0,g0) = 4
    c: DistanceX(g5,g-1) = 150
    c: DistanceY(g-1,g5) = 4.24264
    c: DistanceY(g5,g1) = 2.5
    c: DistanceX(g5,g1) = 2.5
FEATURE [PartDesign::Pad] Pad006  label="padInsertFavGauch"
  AllowMultiFace = false
  BaseFeature = -> Pad005
  Direction = (1,1,1)
  Length = 10
  Length2 = 100
  Profile = -> Sketch017
  Type = 2
FEATURE [Sketcher::SketchObject] Sketch018  label="skPercageInsertFavDroit"
  FullyConstrained = true
  MapMode = 5
  Placement = pos=(0,-71,-2.13e-14) rot=(1,0,0;0.785398rad)
  Support = -> [DatumPlane007]
  expr: Constraints[0] = <<sp>>.insertDiamPercage
  expr: Constraints[1] = <<sp>>.insertFavDistAuZeroDuPLan + <<sp>>.epaisseurParois + <<sp>>.insertFAVDistBord / 2
  expr: Constraints[2] = <<sp>>.epaisseurParois + <<sp>>.insertFAVDistBord / 2
  expr: Constraints[7] = <<sp>>.largeurModuleBase - 2 * <<sp>>.epaisseurParois - <<sp>>.insertFAVDistBord
  sketch-geometry (3):
    g0: Circle CenterX=-6.5 CenterY=10.7426 CenterZ=0 NormalX=0 NormalY=0 NormalZ=1 AngleXU=0 Radius=2
    g1: Circle CenterX=-143.5 CenterY=10.7426 CenterZ=0 NormalX=0 NormalY=0 NormalZ=1 AngleXU=0 Radius=2
    g2: LineSegment StartX=-143.5 StartY=10.7426 StartZ=0 EndX=-6.5 EndY=10.7426 EndZ=0
  constraints (8):
    c: Diameter(g0) = 4
    c: DistanceY(g-1,g0) = 10.7426
    c: DistanceX(g0,g-1) = 6.5
    c: Equal(g0,g1)
    c: Coincident(g2,g1)
    c: Coincident(g2,g0)
    c: Horizontal(g2)
    c: DistanceX(g2,g2) = 137
FEATURE [PartDesign::Pocket] Pocket010  label="trouInsertFavDroit"
  AllowMultiFace = false
  BaseFeature = -> Pad006
  Direction = (1,1,1)
  Length = 8
  Length2 = 100
  Profile = -> Sketch018
  Reversed = true
  Type = 0
  expr: Length = <<sp>>.insertFavProfondeur
FEATURE [PartDesign::Plane] DatumPlane011  label="planFaceAvant"
  AttachmentOffset = pos=(0,0,93.2843) rot=(-1,0,0;0.785398rad)
  Length = 206.452
  MapMode = 5
  Placement = pos=(0,-93.2843,-2.07e-14) rot=(1,0,0;0.785398rad)
  ResizeMode = 0
  Support = -> [XZ_Plane003]
  Width = 172.769
  expr: .AttachmentOffset.Base.z = <<sp>>.planFaceAvant
FEATURE [Sketcher::SketchObject] Sketch030  label="sk_rebordFav"
  FullyConstrained = true
  MapMode = 5
  Placement = pos=(0,-71,-2.13e-14) rot=(1,0,0;0.785398rad)
  Support = -> [DatumPlane007]
  expr: Constraints[0] = <<sp>>.insertFavDistAuZeroDuPLan
  expr: Constraints[19] = <<sp>>.epaisseurParois
  expr: Constraints[20] = <<sp>>.favEpBordure
  expr: Constraints[21] = <<sp>>.favDistBordPlan
  expr: Constraints[22] = <<sp>>.largeurModuleBase - 2 * <<sp>>.epaisseurParois
  expr: Constraints[23] = <<sp>>.favEpBordure
  expr: Constraints[24] = <<sp>>.Face - <<sp>>.epaisseurParois
  expr: Constraints[25] = <<sp>>.favEpBordure
  sketch-geometry (9):
    g0: GeomPoint X=0 Y=4.24264 Z=0
    g1: LineSegment StartX=-147.5 StartY=20.9853 StartZ=0 EndX=-147.5 EndY=81.7426 EndZ=0
    g2: LineSegment StartX=-147.5 StartY=81.7426 StartZ=0 EndX=-2.5 EndY=81.7426 EndZ=0
    g3: LineSegment StartX=-2.5 StartY=81.7426 StartZ=0 EndX=-2.5 EndY=20.9853 EndZ=0
    g4: LineSegment StartX=-2.5 StartY=20.9853 StartZ=0 EndX=-4 EndY=20.9853 EndZ=0
    g5: LineSegment StartX=-4 StartY=20.9853 StartZ=0 EndX=-4 EndY=80.2426 EndZ=0
    g6: LineSegment StartX=-4 StartY=80.2426 StartZ=0 EndX=-146 EndY=80.2426 EndZ=0
    g7: LineSegment StartX=-146 StartY=80.2426 StartZ=0 EndX=-146 EndY=20.9853 EndZ=0
    g8: LineSegment StartX=-146 StartY=20.9853 StartZ=0 EndX=-147.5 EndY=20.9853 EndZ=0
  constraints (26):
    c: DistanceY(g-1,g0) = 4.24264
    c: Vertical(g0,g-1)
    c: Vertical(g1)
    c: Coincident(g1,g2)
    c: Horizontal(g2)
    c: Coincident(g2,g3)
    c: Vertical(g3)
    c: Coincident(g3,g4)
    c: Horizontal(g4)
    c: Coincident(g4,g5)
    c: Vertical(g5)
    c: Coincident(g5,g6)
    c: Horizontal(g6)
    c: Coincident(g6,g7)
    c: Vertical(g7)
    c: Coincident(g7,g8)
    c: Coincident(g8,g1)
    c: Horizontal(g8)
    c: Horizontal(g7,g4)
    c: DistanceX(g3,g0) = 2.5
    c: DistanceX(g4,g4) = 1.5
    c: DistanceY(g0,g3) = 16.7426
    c: DistanceX(g1,g3) = 145
    c: DistanceY(g5,g2) = 1.5
    c: DistanceY(g0,g2) = 77.5
    c: DistanceX(g1,g7) = 1.5
FEATURE [PartDesign::Pad] Pad014  label="favRebordSupport"
  AllowMultiFace = false
  BaseFeature = -> Pocket010
  Direction = (1,1,1)
  Length = 10
  Length2 = 100
  Profile = -> Sketch030
  Type = 3
  UpToFace = -> Pocket010 [Face13]
FEATURE [PartDesign::Pad] Pad015  label="favRebord"
  AllowMultiFace = false
  BaseFeature = -> Pad014
  Direction = (1,1,1)
  Length = 4.15
  Length2 = 100
  Profile = -> Sketch030
  Reversed = true
  Type = 0
  expr: Length = <<sp>>.favBordureProf
FEATURE [Sketcher::SketchObject] Sketch031  label="sk_bourlet"
  ExternalGeometry = -> [Pad015]
  FullyConstrained = true
  MapMode = 5
  Placement = pos=(-2.5,0,0) rot=(0.57735,0.57735,0.57735;2.0944rad)
  Support = -> [Pad015]
  expr: Constraints[3] = <<sp>>.bourletMaintientRayon - <<sp>>.bourletRayonJeu
  sketch-geometry (2):
    g0: ArcOfCircle CenterX=-11.184 CenterY=55.7855 CenterZ=0 NormalX=0 NormalY=0 NormalZ=1 AngleXU=0 Radius=1.3 StartAngle=5.49779 EndAngle=8.63938
    g1: LineSegment StartX=-12.1032 StartY=56.7048 StartZ=0 EndX=-10.2647 EndY=54.8663 EndZ=0
  constraints (6):
    c: Coincident(g0,g-3)
    c: PointOnObject(g0,g-3)
    c: PointOnObject(g0,g-3)
    c: Radius(g0) = 1.3
    c: Coincident(g1,g0)
    c: Coincident(g1,g0)
FEATURE [PartDesign::Pad] Pad016  label="bourlet"
  AllowMultiFace = false
  BaseFeature = -> Pad015
  Direction = (1,1,1)
  Length = 10
  Length2 = 100
  Profile = -> Sketch031
  Reversed = true
  Type = 3
  UpToFace = -> Pad015 [Face11]
FEATURE [Sketcher::SketchObject] Sketch034  label="favTrous001"
  FullyConstrained = true
  MapMode = 5
  Placement = pos=(0,-93.2843,-2.84e-14) rot=(1,0,0;0.785398rad)
  Support = -> [DatumPlane011]
  expr: Constraints[10] = <<sp>>.distZeroPlanFAV
  expr: Constraints[12] = <<favTrous>>.switchPosX
  expr: Constraints[13] = <<favTrous>>.switchPosY
  expr: Constraints[27] = <<favTrous>>.oscilloDistTrousX
  expr: Constraints[28] = <<favTrous>>.oscilloTrouDiam
  expr: Constraints[29] = <<favTrous>>.oscilloDistTrousY
  expr: Constraints[30] = <<favTrous>>.oscilloTrou1PosX
  expr: Constraints[31] = <<favTrous>>.oscilloTrou1PosY
  expr: Constraints[8] = <<SW_C1500AT>>.trouLargeur
  expr: Constraints[9] = <<SW_C1500AT>>.trouLongeur
  sketch-geometry (12):
    g0: LineSegment StartX=-142.55 StartY=88.25 StartZ=0 EndX=-131 EndY=88.25 EndZ=0
    g1: LineSegment StartX=-131 StartY=88.25 StartZ=0 EndX=-131 EndY=60 EndZ=0
    g2: LineSegment StartX=-131 StartY=60 StartZ=0 EndX=-142.55 EndY=60 EndZ=0
    g3: LineSegment StartX=-142.55 StartY=60 StartZ=0 EndX=-142.55 EndY=88.25 EndZ=0
    g4: GeomPoint X=0 Y=20 Z=0
    g5: Circle CenterX=-15 CenterY=27 CenterZ=0 NormalX=0 NormalY=0 NormalZ=1 AngleXU=0 Radius=2
    g6: Circle CenterX=-122 CenterY=27 CenterZ=0 NormalX=0 NormalY=0 NormalZ=1 AngleXU=0 Radius=2
    g7: Circle CenterX=-122 CenterY=93 CenterZ=0 NormalX=0 NormalY=0 NormalZ=1 AngleXU=0 Radius=2
    g8: Circle CenterX=-15 CenterY=93 CenterZ=0 NormalX=0 NormalY=0 NormalZ=1 AngleXU=0 Radius=2
    g9: LineSegment StartX=-122 StartY=93 StartZ=0 EndX=-15 EndY=93 EndZ=0
    g10: LineSegment StartX=-15 StartY=93 StartZ=0 EndX=-15 EndY=27 EndZ=0
    g11: LineSegment StartX=-15 StartY=27 StartZ=0 EndX=-122 EndY=27 EndZ=0
  constraints (32):
    c: Coincident(g0,g1)
    c: Coincident(g1,g2)
    c: Coincident(g2,g3)
    c: Coincident(g3,g0)
    c: Horizontal(g0)
    c: Horizontal(g2)
    c: Vertical(g1)
    c: Vertical(g3)
    c: DistanceX(g0,g0) = 11.55
    c: DistanceY(g1,g1) = 28.25
    c: DistanceY(g-1,g4) = 20
    c: Vertical(g4,g-1)
    c: DistanceX(g1,g4) = 131
    c: DistanceY(g4,g1) = 40
    c: Equal(g8,g7)
    c: Equal(g8,g5)
    c: Equal(g6,g5)
    c: Coincident(g9,g7)
    c: Coincident(g9,g8)
    c: Horizontal(g9)
    c: Coincident(g10,g8)
    c: Coincident(g10,g5)
    c: Vertical(g10)
    c: Coincident(g11,g5)
    c: Coincident(g11,g6)
    c: Horizontal(g11)
    c: Equal(g9,g11)
    c: DistanceX(g9,g9) = 107
    c: Diameter(g8) = 4
    c: DistanceY(g10,g10) = 66
    c: DistanceX(g5,g4) = 15
    c: DistanceY(g4,g5) = 7
FEATURE [PartDesign::Pocket] Pocket016  label="trousFav"
  BaseFeature = -> Pad016
  Direction = (1,1,1)
  Length = 5
  Length2 = 100
  Profile = -> Sketch034
  Type = 1
FEATURE [Sketcher::SketchObject] Sketch035  label="sk_trousAlimSignal"
  FullyConstrained = true
  MapMode = 5
  Placement = pos=(0,-93.2843,-2.84e-14) rot=(1,0,0;0.785398rad)
  Support = -> [DatumPlane011]
  expr: Constraints[0] = <<sp>>.distZeroPlanFAV
  expr: Constraints[2] = <<favTrous>>.oscilloTrouAlimPosX
  expr: Constraints[3] = <<favTrous>>.oscilloTrouAlimPosY
  expr: Constraints[4] = <<favTrous>>.oscilloTrouAlimDiam
  expr: Constraints[5] = <<favTrous>>.bncDiam
  expr: Constraints[6] = <<favTrous>>.signalTrouPosX
  expr: Constraints[7] = <<favTrous>>.signalTrouPosY
  sketch-geometry (3):
    g0: Circle CenterX=-31 CenterY=90 CenterZ=0 NormalX=0 NormalY=0 NormalZ=1 AngleXU=0 Radius=3.5
    g1: GeomPoint X=0 Y=20 Z=0
    g2: Circle CenterX=-111 CenterY=87 CenterZ=0 NormalX=0 NormalY=0 NormalZ=1 AngleXU=0 Radius=5.15
  constraints (8):
    c: DistanceY(g-1,g1) = 20
    c: Vertical(g1,g-1)
    c: DistanceX(g0,g1) = 31
    c: DistanceY(g1,g0) = 70
    c: Diameter(g0) = 7
    c: Diameter(g2) = 10.3
    c: DistanceX(g2,g1) = 111
    c: DistanceY(g1,g2) = 67
FEATURE [PartDesign::Pocket] Pocket017  label="trouSignalEtAlim"
  BaseFeature = -> Pocket016
  Direction = (1,1,1)
  Length = 5
  Length2 = 100
  Profile = -> Sketch035
  Type = 1
FEATURE [Sketcher::SketchObject] Sketch036  label="sk_favTrouBnc"
  FullyConstrained = true
  MapMode = 5
  Placement = pos=(0,-93.2843,-2.84e-14) rot=(1,0,0;0.785398rad)
  Support = -> [DatumPlane011]
  expr: Constraints[0] = <<sp>>.distZeroPlanFAV
  expr: Constraints[2] = <<favTrous>>.bncPosX
  expr: Constraints[3] = <<favTrous>>.bncPosY
  expr: Constraints[4] = <<favTrous>>.bncDiam
  expr: Constraints[8] = <<bnc>>.trouMeplatDepuisLeCentre + <<bnc>>.trouJeu
  sketch-geometry (3):
    g0: ArcOfCircle CenterX=-137 CenterY=42 CenterZ=0 NormalX=0 NormalY=0 NormalZ=1 AngleXU=0 Radius=5.15 StartAngle=0.696659 EndAngle=5.58653
    g1: GeomPoint X=0 Y=20 Z=0
    g2: LineSegment StartX=-133.05 StartY=45.3045 StartZ=0 EndX=-133.05 EndY=38.6955 EndZ=0
  constraints (9):
    c: DistanceY(g-1,g1) = 20
    c: Vertical(g1,g-1)
    c: DistanceX(g0,g1) = 137
    c: DistanceY(g1,g0) = 22
    c: Diameter(g0) = 10.3
    c: Vertical(g2)
    c: Coincident(g0,g2)
    c: Coincident(g0,g2)
    c: DistanceX(g0,g0) = 3.95
FEATURE [PartDesign::Pocket] Pocket018  label="trouBNC"
  BaseFeature = -> Pocket017
  Direction = (1,1,1)
  Length = 5
  Length2 = 100
  Profile = -> Sketch036
  Type = 1
FEATURE [PartDesign::Body] Body002  label="faceAvant"
  BaseFeature = -> Slice_child1
  Group = -> [Clone001,Thickness001,DatumPlane007,Sketch016,Pad005,Sketch017,Pad006,Sketch018,Pocket010,DatumPlane011,Sketch030,Pad014,Pad015,Sketch031,Pad016,Sketch034,Pocket016,Sketch035,Pocket017,Sketch036,Pocket018]
  Origin = -> Origin003
  Tip = -> Pocket018
COMPONENT P2 — recipe-attached ("visTHCM3x10_001", modeled in this document).
Construction recipe (the document's own serialized feature program — sketch geometry with constraints, then the solid features built on it; lengths are millimeters unless a unit is written):

FEATURE [Sketcher::SketchObject] Sketch020
  FullyConstrained = false
  MapMode = 5
  Support = -> [XY_Plane006]
  sketch-geometry (1):
    g0: Circle CenterX=0 CenterY=0 CenterZ=0 NormalX=0 NormalY=0 NormalZ=1 AngleXU=0 Radius=2.75
  constraints (2):
    c: Coincident(g0,g-1)
    c: Diameter(g0) = 5.5
FEATURE [PartDesign::Pad] Pad008  label="tete"
  AllowMultiFace = false
  Direction = (1,1,1)
  Length = 3
  Length2 = 100
  Profile = -> Sketch020
  Type = 0
FEATURE [Sketcher::SketchObject] Sketch001
  FullyConstrained = false
  MapMode = 5
  Placement = pos=(0,0,0) rot=(1,0,0;3.14159rad)
  Support = -> [Pad008]
  sketch-geometry (1):
    g0: Circle CenterX=0 CenterY=0 CenterZ=0 NormalX=0 NormalY=0 NormalZ=1 AngleXU=0 Radius=1.5
  constraints (2):
    c: Coincident(g0,g-1)
    c: Diameter(g0) = 3
FEATURE [PartDesign::Pad] Pad009  label="corps"
  AllowMultiFace = false
  BaseFeature = -> Pad008
  Direction = (1,1,1)
  Length = 10
  Length2 = 100
  Profile = -> Sketch001
  Type = 0
FEATURE [PartDesign::Plane] DatumPlane008
  AttachmentOffset = pos=(0,0,3) rot=(0,0,1;0rad)
  Length = 60
  MapMode = 5
  Placement = pos=(0,0,3) rot=(0,0,1;0rad)
  ResizeMode = 0
  Support = -> [XY_Plane006]
  Width = 60
FEATURE [Sketcher::SketchObject] Sketch021
  FullyConstrained = false
  MapMode = 5
  Placement = pos=(0,0,3) rot=(0,0,1;0rad)
  Support = -> [DatumPlane008]
  sketch-geometry (7):
    g0: LineSegment StartX=0.721688 StartY=-1.25 StartZ=0 EndX=1.44338 EndY=1.0119e-12 EndZ=0
    g1: LineSegment StartX=1.44338 StartY=1.0119e-12 StartZ=0 EndX=0.721688 EndY=1.25 EndZ=0
    g2: LineSegment StartX=0.721688 StartY=1.25 StartZ=0 EndX=-0.721688 EndY=1.25 EndZ=0
    g3: LineSegment StartX=-0.721688 StartY=1.25 StartZ=0 EndX=-1.44338 EndY=8.689e-13 EndZ=0
    g4: LineSegment StartX=-1.44338 StartY=8.689e-13 StartZ=0 EndX=-0.721688 EndY=-1.25 EndZ=0
    g5: LineSegment StartX=-0.721688 StartY=-1.25 StartZ=0 EndX=0.721688 EndY=-1.25 EndZ=0
    g6: Circle CenterX=0 CenterY=0 CenterZ=0 NormalX=0 NormalY=0 NormalZ=1 AngleXU=0 Radius=1.44338
  constraints (16):
    c: Coincident(g0,g1)
    c: Coincident(g1,g2)
    c: Coincident(g2,g3)
    c: Coincident(g3,g4)
    c: Coincident(g4,g5)
    c: Coincident(g5,g0)
    c: Equal(g0, g1-g5) x5
    c: PointOnObject(g0,g6)
    c: PointOnObject(g1,g6)
    c: PointOnObject(g2,g6)
    c: PointOnObject(g3,g6)
    c: PointOnObject(g4,g6)
    c: PointOnObject(g5,g6)
    c: Coincident(g6,g-1)
    c: Horizontal(g2)
    c: DistanceY(g0,g1) = 2.5
FEATURE [PartDesign::Pocket] Pocket011  label="emprunte"
  AllowMultiFace = false
  BaseFeature = -> Pad009
  Direction = (1,1,1)
  Length = 4
  Length2 = 100
  Profile = -> Sketch021
  Type = 0
FEATURE [PartDesign::Body] Body003  label="visTHCM3x10_001"
  Group = -> [Sketch020,Pad008,Sketch001,Pad009,DatumPlane008,Sketch021,Pocket011]
  Origin = -> Origin010
  Placement = pos=(-6.5,-61.582,5.72756) rot=(1,0,0;3.92699rad)
  Tip = -> Pocket011
COMPONENT P3 — recipe-attached ("visTHCM3x10_002", modeled in this document).
Construction recipe (the document's own serialized feature program — sketch geometry with constraints, then the solid features built on it; lengths are millimeters unless a unit is written):

FEATURE [PartDesign::Plane] DatumPlane009
  AttachmentOffset = pos=(0,0,3) rot=(0,0,1;0rad)
  Length = 60
  MapMode = 5
  Placement = pos=(0,0,3) rot=(0,0,1;0rad)
  ResizeMode = 0
  Support = -> [XY_Plane007]
  Width = 60
FEATURE [Sketcher::SketchObject] Sketch022
  FullyConstrained = false
  MapMode = 5
  Support = -> [XY_Plane007]
  sketch-geometry (1):
    g0: Circle CenterX=0 CenterY=0 CenterZ=0 NormalX=0 NormalY=0 NormalZ=1 AngleXU=0 Radius=2.75
  constraints (2):
    c: Coincident(g0,g-1)
    c: Diameter(g0) = 5.5
FEATURE [PartDesign::Pad] Pad011  label="tete001"
  AllowMultiFace = false
  Direction = (1,1,1)
  Length = 3
  Length2 = 100
  Profile = -> Sketch022
  Type = 0
FEATURE [Sketcher::SketchObject] Sketch023
  FullyConstrained = false
  MapMode = 5
  Placement = pos=(0,0,0) rot=(1,0,0;3.14159rad)
  Support = -> [Pad011]
  sketch-geometry (1):
    g0: Circle CenterX=0 CenterY=0 CenterZ=0 NormalX=0 NormalY=0 NormalZ=1 AngleXU=0 Radius=1.5
  constraints (2):
    c: Coincident(g0,g-1)
    c: Diameter(g0) = 3
FEATURE [PartDesign::Pad] Pad010  label="corps001"
  AllowMultiFace = false
  BaseFeature = -> Pad011
  Direction = (1,1,1)
  Length = 10
  Length2 = 100
  Profile = -> Sketch023
  Type = 0
FEATURE [Sketcher::SketchObject] Sketch024
  FullyConstrained = false
  MapMode = 5
  Placement = pos=(0,0,3) rot=(0,0,1;0rad)
  Support = -> [DatumPlane009]
  sketch-geometry (7):
    g0: LineSegment StartX=0.721688 StartY=-1.25 StartZ=0 EndX=1.44338 EndY=1.0119e-12 EndZ=0
    g1: LineSegment StartX=1.44338 StartY=1.0119e-12 StartZ=0 EndX=0.721688 EndY=1.25 EndZ=0
    g2: LineSegment StartX=0.721688 StartY=1.25 StartZ=0 EndX=-0.721688 EndY=1.25 EndZ=0
    g3: LineSegment StartX=-0.721688 StartY=1.25 StartZ=0 EndX=-1.44338 EndY=8.689e-13 EndZ=0
    g4: LineSegment StartX=-1.44338 StartY=8.689e-13 StartZ=0 EndX=-0.721688 EndY=-1.25 EndZ=0
    g5: LineSegment StartX=-0.721688 StartY=-1.25 StartZ=0 EndX=0.721688 EndY=-1.25 EndZ=0
    g6: Circle CenterX=0 CenterY=0 CenterZ=0 NormalX=0 NormalY=0 NormalZ=1 AngleXU=0 Radius=1.44338
  constraints (16):
    c: Coincident(g0,g1)
    c: Coincident(g1,g2)
    c: Coincident(g2,g3)
    c: Coincident(g3,g4)
    c: Coincident(g4,g5)
    c: Coincident(g5,g0)
    c: Equal(g0, g1-g5) x5
    c: PointOnObject(g0,g6)
    c: PointOnObject(g1,g6)
    c: PointOnObject(g2,g6)
    c: PointOnObject(g3,g6)
    c: PointOnObject(g4,g6)
    c: PointOnObject(g5,g6)
    c: Coincident(g6,g-1)
    c: Horizontal(g2)
    c: DistanceY(g0,g1) = 2.5
FEATURE [PartDesign::Pocket] Pocket012  label="emprunte001"
  AllowMultiFace = false
  BaseFeature = -> Pad010
  Direction = (1,1,1)
  Length = 4
  Length2 = 100
  Profile = -> Sketch024
  Type = 0
FEATURE [PartDesign::Body] Body004  label="visTHCM3x10_002"
  Group = -> [Sketch022,Pad011,Sketch023,Pad010,DatumPlane009,Sketch024,Pocket012]
  Origin = -> Origin011
  Placement = pos=(-143.5,-61.582,5.72756) rot=(1,0,0;3.92699rad)
  Tip = -> Pocket012
COMPONENT P4 — recipe-attached ("visTHCM3x6_FAV001", modeled in this document).
Construction recipe (the document's own serialized feature program — sketch geometry with constraints, then the solid features built on it; lengths are millimeters unless a unit is written):

FEATURE [Sketcher::SketchObject] Sketch047
  FullyConstrained = false
  MapMode = 5
  Support = -> [XY_Plane046]
  sketch-geometry (1):
    g0: Circle CenterX=0 CenterY=0 CenterZ=0 NormalX=0 NormalY=0 NormalZ=1 AngleXU=0 Radius=2.75
  constraints (2):
    c: Coincident(g0,g-1)
    c: Diameter(g0) = 5.5
FEATURE [PartDesign::Pad] Pad024  label="tete004"
  AllowMultiFace = false
  Direction = (1,1,1)
  Length = 3
  Length2 = 100
  Profile = -> Sketch047
  Type = 0
FEATURE [Sketcher::SketchObject] Sketch048
  FullyConstrained = false
  MapMode = 5
  Placement = pos=(0,0,0) rot=(1,0,0;3.14159rad)
  Support = -> [Pad024]
  sketch-geometry (1):
    g0: Circle CenterX=0 CenterY=0 CenterZ=0 NormalX=0 NormalY=0 NormalZ=1 AngleXU=0 Radius=1.5
  constraints (2):
    c: Coincident(g0,g-1)
    c: Diameter(g0) = 3
FEATURE [PartDesign::Pad] Pad025  label="corps004"
  AllowMultiFace = false
  BaseFeature = -> Pad024
  Direction = (1,1,1)
  Length = 6
  Length2 = 100
  Profile = -> Sketch048
  Type = 0
FEATURE [PartDesign::Plane] DatumPlane018
  AttachmentOffset = pos=(0,0,3) rot=(0,0,1;0rad)
  Length = 60
  MapMode = 5
  Placement = pos=(0,0,3) rot=(0,0,1;0rad)
  ResizeMode = 0
  Support = -> [XY_Plane046]
  Width = 60
FEATURE [Sketcher::SketchObject] Sketch049
  FullyConstrained = false
  MapMode = 5
  Placement = pos=(0,0,3) rot=(0,0,1;0rad)
  Support = -> [DatumPlane018]
  sketch-geometry (7):
    g0: LineSegment StartX=0.721688 StartY=-1.25 StartZ=0 EndX=1.44338 EndY=1.0119e-12 EndZ=0
    g1: LineSegment StartX=1.44338 StartY=1.0119e-12 StartZ=0 EndX=0.721688 EndY=1.25 EndZ=0
    g2: LineSegment StartX=0.721688 StartY=1.25 StartZ=0 EndX=-0.721688 EndY=1.25 EndZ=0
    g3: LineSegment StartX=-0.721688 StartY=1.25 StartZ=0 EndX=-1.44338 EndY=8.689e-13 EndZ=0
    g4: LineSegment StartX=-1.44338 StartY=8.689e-13 StartZ=0 EndX=-0.721688 EndY=-1.25 EndZ=0
    g5: LineSegment StartX=-0.721688 StartY=-1.25 StartZ=0 EndX=0.721688 EndY=-1.25 EndZ=0
    g6: Circle CenterX=0 CenterY=0 CenterZ=0 NormalX=0 NormalY=0 NormalZ=1 AngleXU=0 Radius=1.44338
  constraints (16):
    c: Coincident(g0,g1)
    c: Coincident(g1,g2)
    c: Coincident(g2,g3)
    c: Coincident(g3,g4)
    c: Coincident(g4,g5)
    c: Coincident(g5,g0)
    c: Equal(g0, g1-g5) x5
    c: PointOnObject(g0,g6)
    c: PointOnObject(g1,g6)
    c: PointOnObject(g2,g6)
    c: PointOnObject(g3,g6)
    c: PointOnObject(g4,g6)
    c: PointOnObject(g5,g6)
    c: Coincident(g6,g-1)
    c: Horizontal(g2)
    c: DistanceY(g0,g1) = 2.5
FEATURE [PartDesign::Pocket] Pocket022  label="emprunte004"
  AllowMultiFace = false
  BaseFeature = -> Pad025
  Direction = (1,1,1)
  Length = 4
  Length2 = 100
  Profile = -> Sketch049
  Type = 0
FEATURE [PartDesign::Body] Body013  label="visTHCM3x6_FAV001"
  Group = -> [Sketch047,Pad024,Sketch048,Pad025,DatumPlane018,Sketch049,Pocket022]
  Origin = -> Origin048
  Placement = pos=(-6.46,-61.9464,6.08988) rot=(1,0,0;3.92699rad)
  Tip = -> Pocket022
COMPONENT P5 — recipe-attached ("visTHCM3x6_FAV002", modeled in this document).
Construction recipe (the document's own serialized feature program — sketch geometry with constraints, then the solid features built on it; lengths are millimeters unless a unit is written):

FEATURE [PartDesign::Plane] DatumPlane019
  AttachmentOffset = pos=(0,0,3) rot=(0,0,1;0rad)
  Length = 60
  MapMode = 5
  Placement = pos=(0,0,3) rot=(0,0,1;0rad)
  ResizeMode = 0
  Support = -> [XY_Plane047]
  Width = 60
FEATURE [Sketcher::SketchObject] Sketch051
  FullyConstrained = false
  MapMode = 5
  Support = -> [XY_Plane047]
  sketch-geometry (1):
    g0: Circle CenterX=0 CenterY=0 CenterZ=0 NormalX=0 NormalY=0 NormalZ=1 AngleXU=0 Radius=2.75
  constraints (2):
    c: Coincident(g0,g-1)
    c: Diameter(g0) = 5.5
FEATURE [PartDesign::Pad] Pad027  label="tete005"
  AllowMultiFace = false
  Direction = (1,1,1)
  Length = 3
  Length2 = 100
  Profile = -> Sketch051
  Type = 0
FEATURE [Sketcher::SketchObject] Sketch050
  FullyConstrained = false
  MapMode = 5
  Placement = pos=(0,0,0) rot=(1,0,0;3.14159rad)
  Support = -> [Pad027]
  sketch-geometry (1):
    g0: Circle CenterX=0 CenterY=0 CenterZ=0 NormalX=0 NormalY=0 NormalZ=1 AngleXU=0 Radius=1.5
  constraints (2):
    c: Coincident(g0,g-1)
    c: Diameter(g0) = 3
FEATURE [PartDesign::Pad] Pad026  label="corps005"
  AllowMultiFace = false
  BaseFeature = -> Pad027
  Direction = (1,1,1)
  Length = 6
  Length2 = 100
  Profile = -> Sketch050
  Type = 0
FEATURE [Sketcher::SketchObject] Sketch052
  FullyConstrained = false
  MapMode = 5
  Placement = pos=(0,0,3) rot=(0,0,1;0rad)
  Support = -> [DatumPlane019]
  sketch-geometry (7):
    g0: LineSegment StartX=0.721688 StartY=-1.25 StartZ=0 EndX=1.44338 EndY=1.0119e-12 EndZ=0
    g1: LineSegment StartX=1.44338 StartY=1.0119e-12 StartZ=0 EndX=0.721688 EndY=1.25 EndZ=0
    g2: LineSegment StartX=0.721688 StartY=1.25 StartZ=0 EndX=-0.721688 EndY=1.25 EndZ=0
    g3: LineSegment StartX=-0.721688 StartY=1.25 StartZ=0 EndX=-1.44338 EndY=8.689e-13 EndZ=0
    g4: LineSegment StartX=-1.44338 StartY=8.689e-13 StartZ=0 EndX=-0.721688 EndY=-1.25 EndZ=0
    g5: LineSegment StartX=-0.721688 StartY=-1.25 StartZ=0 EndX=0.721688 EndY=-1.25 EndZ=0
    g6: Circle CenterX=0 CenterY=0 CenterZ=0 NormalX=0 NormalY=0 NormalZ=1 AngleXU=0 Radius=1.44338
  constraints (16):
    c: Coincident(g0,g1)
    c: Coincident(g1,g2)
    c: Coincident(g2,g3)
    c: Coincident(g3,g4)
    c: Coincident(g4,g5)
    c: Coincident(g5,g0)
    c: Equal(g0, g1-g5) x5
    c: PointOnObject(g0,g6)
    c: PointOnObject(g1,g6)
    c: PointOnObject(g2,g6)
    c: PointOnObject(g3,g6)
    c: PointOnObject(g4,g6)
    c: PointOnObject(g5,g6)
    c: Coincident(g6,g-1)
    c: Horizontal(g2)
    c: DistanceY(g0,g1) = 2.5
FEATURE [PartDesign::Pocket] Pocket023  label="emprunte005"
  AllowMultiFace = false
  BaseFeature = -> Pad026
  Direction = (1,1,1)
  Length = 4
  Length2 = 100
  Profile = -> Sketch052
  Type = 0
FEATURE [PartDesign::Body] Body014  label="visTHCM3x6_FAV002"
  Group = -> [Sketch051,Pad027,Sketch050,Pad026,DatumPlane019,Sketch052,Pocket023]
  Origin = -> Origin049
  Placement = pos=(-143.48,-61.9464,6.08988) rot=(1,0,0;3.92699rad)
  Tip = -> Pocket023
COMPONENT P6 — recipe-attached ("capot", modeled in this document).
Construction recipe (the document's own serialized feature program — sketch geometry with constraints, then the solid features built on it; lengths are millimeters unless a unit is written):

FEATURE [Sketcher::SketchObject] Sketch  label="profileDeBase"
  FullyConstrained = true
  MapMode = 5
  Placement = pos=(0,0,0) rot=(0.57735,0.57735,0.57735;2.0944rad)
  Support = -> [YZ_Plane001]
  expr: Constraints[10] = <<sp>>.petitRetour
  expr: Constraints[11] = <<sp>>.angleFacePetitRetour
  expr: Constraints[12] = <<sp>>.Face
  expr: Constraints[13] = <<sp>>.angleFaceRetourHaut
  expr: Constraints[8] = <<sp>>.Base
  expr: Constraints[9] = <<sp>>.anglePetitRetourBase
  sketch-geometry (5):
    g0: LineSegment StartX=0 StartY=0 StartZ=0 EndX=-65 EndY=0 EndZ=0
    g1: LineSegment StartX=-65 StartY=0 StartZ=0 EndX=-79.1421 EndY=14.1421 EndZ=0
    g2: LineSegment StartX=-79.1421 StartY=14.1421 StartZ=0 EndX=-22.5736 EndY=70.7107 EndZ=0
    g3: LineSegment StartX=-22.5736 StartY=70.7107 StartZ=0 EndX=0 EndY=48.1371 EndZ=0
    g4: LineSegment StartX=0 StartY=48.1371 StartZ=0 EndX=0 EndY=0 EndZ=0
  constraints (14):
    c: Coincident(g-1,g0)
    c: Horizontal(g0)
    c: Coincident(g0,g1)
    c: Coincident(g1,g2)
    c: Coincident(g2,g3)
    c: PointOnObject(g3,g-2)
    c: Coincident(g3,g4)
    c: Coincident(g4,g0)
    c: DistanceX(g0,g0) = 65
    c: Angle(g0,g1) = 2.35619
    c: Distance(g1) = 20
    c: Angle(g1,g2) = 1.5708
    c: Distance(g2) = 80
    c: Angle(g2,g3) = 1.5708
FEATURE [PartDesign::Pad] Pad
  AllowMultiFace = false
  Direction = (1,1,1)
  Length = 150
  Length2 = 100
  Placement = pos=(0,0,0) rot=(0.57735,0.57735,0.57735;2.0944rad)
  Profile = -> Sketch
  Reversed = true
  Type = 0
  expr: Length = <<sp>>.largeurModuleBase
FEATURE [PartDesign::Plane] DatumPlane
  AttachmentOffset = pos=(71,0,0) rot=(0,-1,0;0.785398rad)
  Length = 98.6412
  MapMode = 5
  Placement = pos=(-7.9e-15,8e-15,71) rot=(0.678598,0.678598,0.281085;3.68962rad)
  ResizeMode = 0
  Support = -> [Pad]
  Width = 63.0813
FEATURE [PartDesign::Body] Body  label="Base"
  Group = -> [Sketch,Pad,DatumPlane]
  Origin = -> Origin001
  Tip = -> Pad
COMPONENT P7 — geometry summary ("xt60fem"; no construction recipe available for this part):
  bounding box: 20.5 x 16.5 x 7.5 mm
  tessellated surface: 17,936 triangles
  volume: 955 mm^3 (38% of its bounding box)
COMPONENT P8 — geometry summary ("xt60Male"; no construction recipe available for this part):
  bounding box: 20.2 x 16.6 x 7.5 mm
  tessellated surface: 13,112 triangles
  volume: 1201 mm^3 (48% of its bounding box)
COMPONENT P9 — geometry summary ("ZSB_RUTHEX_M3_5.7_001"; no construction recipe available for this part):
  bounding box: 5.7 x 4.6 x 4.6 mm
  tessellated surface: 4,592 triangles
  volume: 44 mm^3 (36% of its bounding box)
  symmetry: 4-fold rotationally symmetric about the y axis; mirror-symmetric across its x mid-plane, z mid-plane
COMPONENT P10 — geometry summary ("ZSB_RUTHEX_M3_5.7_002"; no construction recipe available for this part):
  bounding box: 5.7 x 4.6 x 4.6 mm
  tessellated surface: 4,592 triangles
  volume: 44 mm^3 (36% of its bounding box)
  symmetry: 4-fold rotationally symmetric about the y axis; mirror-symmetric across its x mid-plane, z mid-plane
COMPONENT P11 — geometry summary ("ZSB_RUTHEX_M3_5.7_003"; no construction recipe available for this part):
  bounding box: 6.9 x 6.9 x 4.6 mm
  tessellated surface: 4,592 triangles
  volume: 44 mm^3 (20% of its bounding box)
  symmetry: mirror-symmetric across its x mid-plane
COMPONENT P12 — geometry summary ("ZSB_RUTHEX_M3_5.7_004"; no construction recipe available for this part):
  bounding box: 6.9 x 6.9 x 4.6 mm
  tessellated surface: 4,592 triangles
  volume: 44 mm^3 (20% of its bounding box)
  symmetry: mirror-symmetric across its x mid-plane
COMPONENT P13 — recipe-attached ("partVisPointeauM3x10_001", modeled in this document).
Construction recipe (the document's own serialized feature program — sketch geometry with constraints, then the solid features built on it; lengths are millimeters unless a unit is written):

FEATURE [Sketcher::SketchObject] Sketch025
  FullyConstrained = false
  MapMode = 5
  Support = -> [XY_Plane008]
  sketch-geometry (1):
    g0: Circle CenterX=0 CenterY=0 CenterZ=0 NormalX=0 NormalY=0 NormalZ=1 AngleXU=0 Radius=1.5
  constraints (2):
    c: Coincident(g0,g-1)
    c: Diameter(g0) = 3
FEATURE [Sketcher::SketchObject] Sketch026
  FullyConstrained = false
  MapMode = 5
  Support = -> [XY_Plane008]
  sketch-geometry (7):
    g0: LineSegment StartX=0.433013 StartY=-0.75 StartZ=0 EndX=0.866025 EndY=1.25568e-11 EndZ=0
    g1: LineSegment StartX=0.866025 StartY=1.25568e-11 StartZ=0 EndX=0.433013 EndY=0.75 EndZ=0
    g2: LineSegment StartX=0.433013 StartY=0.75 StartZ=0 EndX=-0.433013 EndY=0.75 EndZ=0
    g3: LineSegment StartX=-0.433013 StartY=0.75 StartZ=0 EndX=-0.866025 EndY=2.91366e-11 EndZ=0
    g4: LineSegment StartX=-0.866025 StartY=2.91366e-11 StartZ=0 EndX=-0.433013 EndY=-0.75 EndZ=0
    g5: LineSegment StartX=-0.433013 StartY=-0.75 StartZ=0 EndX=0.433013 EndY=-0.75 EndZ=0
    g6: Circle CenterX=0 CenterY=0 CenterZ=0 NormalX=0 NormalY=0 NormalZ=1 AngleXU=0 Radius=0.866025
  constraints (16):
    c: Coincident(g0,g1)
    c: Coincident(g1,g2)
    c: Coincident(g2,g3)
    c: Coincident(g3,g4)
    c: Coincident(g4,g5)
    c: Coincident(g5,g0)
    c: Equal(g0, g1-g5) x5
    c: PointOnObject(g0,g6)
    c: PointOnObject(g1,g6)
    c: PointOnObject(g2,g6)
    c: PointOnObject(g3,g6)
    c: PointOnObject(g4,g6)
    c: PointOnObject(g5,g6)
    c: Coincident(g6,g-1)
    c: Horizontal(g2)
    c: DistanceY(g0,g1) = 1.5
FEATURE [PartDesign::Pad] Pad012
  AllowMultiFace = false
  Direction = (1,1,1)
  Length = 10
  Length2 = 100
  Profile = -> Sketch025
  Type = 0
FEATURE [PartDesign::Chamfer] Chamfer
  Angle = 45
  Base = -> Pad012 [Edge3]
  BaseFeature = -> Pad012
  ChamferType = 0
  FlipDirection = false
  Size = 1.4
  Size2 = 1
  SupportTransform = false
  UseAllEdges = false
FEATURE [PartDesign::Pocket] Pocket013
  AllowMultiFace = false
  BaseFeature = -> Chamfer
  Direction = (1,1,1)
  Length = 1.5
  Length2 = 100
  Profile = -> Sketch026
  Reversed = true
  Type = 0
FEATURE [PartDesign::Chamfer] Chamfer001
  Angle = 45
  Base = -> Pocket013 [Edge3]
  BaseFeature = -> Pocket013
  ChamferType = 0
  FlipDirection = false
  Size = 0.1
  Size2 = 1
  SupportTransform = false
  UseAllEdges = false
FEATURE [PartDesign::Body] Body005  label="bodyVisPointeauM3x10_001"
  Group = -> [Sketch025,Pad012,Chamfer,Sketch026,Pocket013,Chamfer001]
  Origin = -> Origin013
  Tip = -> Chamfer001
COMPONENT P14 — recipe-attached ("partVisPointeauM3x10_002", modeled in this document).
Construction recipe (the document's own serialized feature program — sketch geometry with constraints, then the solid features built on it; lengths are millimeters unless a unit is written):

FEATURE [Sketcher::SketchObject] Sketch027
  FullyConstrained = false
  MapMode = 5
  Support = -> [XY_Plane010]
  sketch-geometry (7):
    g0: LineSegment StartX=0.433013 StartY=-0.75 StartZ=0 EndX=0.866025 EndY=1.25568e-11 EndZ=0
    g1: LineSegment StartX=0.866025 StartY=1.25568e-11 StartZ=0 EndX=0.433013 EndY=0.75 EndZ=0
    g2: LineSegment StartX=0.433013 StartY=0.75 StartZ=0 EndX=-0.433013 EndY=0.75 EndZ=0
    g3: LineSegment StartX=-0.433013 StartY=0.75 StartZ=0 EndX=-0.866025 EndY=2.91366e-11 EndZ=0
    g4: LineSegment StartX=-0.866025 StartY=2.91366e-11 StartZ=0 EndX=-0.433013 EndY=-0.75 EndZ=0
    g5: LineSegment StartX=-0.433013 StartY=-0.75 StartZ=0 EndX=0.433013 EndY=-0.75 EndZ=0
    g6: Circle CenterX=0 CenterY=0 CenterZ=0 NormalX=0 NormalY=0 NormalZ=1 AngleXU=0 Radius=0.866025
  constraints (16):
    c: Coincident(g0,g1)
    c: Coincident(g1,g2)
    c: Coincident(g2,g3)
    c: Coincident(g3,g4)
    c: Coincident(g4,g5)
    c: Coincident(g5,g0)
    c: Equal(g0, g1-g5) x5
    c: PointOnObject(g0,g6)
    c: PointOnObject(g1,g6)
    c: PointOnObject(g2,g6)
    c: PointOnObject(g3,g6)
    c: PointOnObject(g4,g6)
    c: PointOnObject(g5,g6)
    c: Coincident(g6,g-1)
    c: Horizontal(g2)
    c: DistanceY(g0,g1) = 1.5
FEATURE [Sketcher::SketchObject] Sketch028
  FullyConstrained = false
  MapMode = 5
  Support = -> [XY_Plane010]
  sketch-geometry (1):
    g0: Circle CenterX=0 CenterY=0 CenterZ=0 NormalX=0 NormalY=0 NormalZ=1 AngleXU=0 Radius=1.5
  constraints (2):
    c: Coincident(g0,g-1)
    c: Diameter(g0) = 3
FEATURE [PartDesign::Pad] Pad013
  AllowMultiFace = false
  Direction = (1,1,1)
  Length = 10
  Length2 = 100
  Profile = -> Sketch028
  Type = 0
FEATURE [PartDesign::Chamfer] Chamfer003
  Angle = 45
  Base = -> Pad013 [Edge3]
  BaseFeature = -> Pad013
  ChamferType = 0
  FlipDirection = false
  Size = 1.4
  Size2 = 1
  SupportTransform = false
  UseAllEdges = false
FEATURE [PartDesign::Pocket] Pocket014
  AllowMultiFace = false
  BaseFeature = -> Chamfer003
  Direction = (1,1,1)
  Length = 1.5
  Length2 = 100
  Profile = -> Sketch027
  Reversed = true
  Type = 0
FEATURE [PartDesign::Chamfer] Chamfer002
  Angle = 45
  Base = -> Pocket014 [Edge3]
  BaseFeature = -> Pocket014
  ChamferType = 0
  FlipDirection = false
  Size = 0.1
  Size2 = 1
  SupportTransform = false
  UseAllEdges = false
FEATURE [PartDesign::Body] Body006  label="bodyVisPointeauM3x10_002"
  Group = -> [Sketch028,Pad013,Chamfer003,Sketch027,Pocket014,Chamfer002]
  Origin = -> Origin015
  Tip = -> Chamfer002
COMPONENT P15 — recipe-attached ("tigeLaiton001", modeled in this document).
Construction recipe (the document's own serialized feature program — sketch geometry with constraints, then the solid features built on it; lengths are millimeters unless a unit is written):

FEATURE [PartDesign::Plane] DatumPlane012  label="planBaseTige"
  AttachmentOffset = pos=(0,0,-5.18) rot=(0,0,1;0rad)
  Length = 60
  MapMode = 5
  Placement = pos=(-5.18,1.2e-15,-1.2e-15) rot=(0.57735,0.57735,0.57735;2.0944rad)
  ResizeMode = 0
  Support = -> [YZ_Plane012]
  Width = 60
  expr: .AttachmentOffset.Base.z = -<<tige>>.planBaseTigeposX
FEATURE [Sketcher::SketchObject] Sketch032  label="sk_tiges"
  FullyConstrained = true
  MapMode = 5
  Placement = pos=(-5.18,1.2e-15,-1.2e-15) rot=(0.57735,0.57735,0.57735;2.0944rad)
  Support = -> [DatumPlane012]
  expr: Constraints[0] = <<tige>>.tigeDiam
  expr: Constraints[1] = <<tige>>.tigePosY
  expr: Constraints[2] = <<tige>>.tigePosX
  sketch-geometry (1):
    g0: Circle CenterX=-14 CenterY=14.3 CenterZ=0 NormalX=0 NormalY=0 NormalZ=1 AngleXU=0 Radius=1.25
  constraints (3):
    c: Diameter(g0) = 2.5
    c: DistanceY(g-1,g0) = 14.3
    c: DistanceX(g0,g-1) = 14
FEATURE [PartDesign::Pad] Pad017  label="tigeBasse"
  AllowMultiFace = false
  Direction = (1,1,1)
  Length = 133.62
  Length2 = 100
  Placement = pos=(-5.18,1e-15,-1e-15) rot=(0.57735,0.57735,0.57735;2.0944rad)
  Profile = -> Sketch032
  Reversed = true
  Type = 0
  expr: Length = <<tige>>.tigeLong
FEATURE [PartDesign::Body] Body007  label="tigeLaiton"
  Group = -> [DatumPlane012,Sketch032,Pad017]
  Origin = -> Origin016
  Tip = -> Pad017
FEATURE [PartDesign::Plane] DatumPlane013  label="planTige2"
  AttachmentOffset = pos=(0,0,-5.18) rot=(0,0,1;0rad)
  Length = 60
  MapMode = 5
  Placement = pos=(-5.18,1.2e-15,-1.2e-15) rot=(0.57735,0.57735,0.57735;2.0944rad)
  ResizeMode = 0
  Support = -> [YZ_Plane014]
  Width = 60
  expr: .AttachmentOffset.Base.z = -<<tige>>.planBaseTigeposX
FEATURE [Sketcher::SketchObject] Sketch033  label="sk_tige2"
  FullyConstrained = true
  MapMode = 5
  Placement = pos=(-5.18,1.2e-15,-1.2e-15) rot=(0.57735,0.57735,0.57735;2.0944rad)
  Support = -> [DatumPlane013]
  expr: Constraints[0] = <<tige>>.tigeDiam
  expr: Constraints[1] = <<tige>>.tigePosX
  expr: Constraints[2] = <<tige>>.tigePosY + <<tige>>.xtEcartBroches
  sketch-geometry (1):
    g0: Circle CenterX=-14 CenterY=21.86 CenterZ=0 NormalX=0 NormalY=0 NormalZ=1 AngleXU=0 Radius=1.25
  constraints (3):
    c: Diameter(g0) = 2.5
    c: DistanceX(g0,g-1) = 14
    c: DistanceY(g-1,g0) = 21.86
FEATURE [PartDesign::Pad] Pad018
  AllowMultiFace = false
  Direction = (1,1,1)
  Length = 133.62
  Length2 = 100
  Placement = pos=(-5.18,1e-15,-1e-15) rot=(0.57735,0.57735,0.57735;2.0944rad)
  Profile = -> Sketch033
  Reversed = true
  Type = 0
  expr: Length = <<tige>>.tigeLong
FEATURE [PartDesign::Body] Body008  label="tige2"
  Group = -> [DatumPlane013,Sketch033,Pad018]
  Origin = -> Origin018
  Tip = -> Pad018
COMPONENT P16 — recipe-attached ("BNC_embase", modeled in this document).
Construction recipe (the document's own serialized feature program — sketch geometry with constraints, then the solid features built on it; lengths are millimeters unless a unit is written):

FEATURE [Sketcher::SketchObject] Sketch037  label="sk_trou"
  FullyConstrained = true
  MapMode = 5
  Support = -> [XY_Plane041]
  expr: Constraints[1] = <<bnc>>.trouDiam + <<bnc>>.trouJeu
  expr: Constraints[5] = <<bnc>>.trouMeplatDepuisLeCentre + <<bnc>>.trouJeu
  sketch-geometry (2):
    g0: ArcOfCircle CenterX=0 CenterY=0 CenterZ=0 NormalX=0 NormalY=0 NormalZ=1 AngleXU=0 Radius=5.15 StartAngle=0.696659 EndAngle=5.58653
    g1: LineSegment StartX=3.95 StartY=3.30454 StartZ=0 EndX=3.95 EndY=-3.30454 EndZ=0
  constraints (6):
    c: Coincident(g0,g-1)
    c: Diameter(g0) = 10.3
    c: Vertical(g1)
    c: Coincident(g0,g1)
    c: Coincident(g0,g1)
    c: DistanceX(g0,g0) = 3.95
FEATURE [PartDesign::Body] Body009  label="bncBodyPourTrou"
  Group = -> [Sketch037]
  Origin = -> Origin041
COMPONENT P17 — recipe-attached ("groupeDCDC", modeled in this document).
Construction recipe (the document's own serialized feature program — sketch geometry with constraints, then the solid features built on it; lengths are millimeters unless a unit is written):

FEATURE [Sketcher::SketchObject] Sketch041
  FullyConstrained = false
  MapMode = 5
  Support = -> [XY_Plane044]
  sketch-geometry (1):
    g0: Circle CenterX=0 CenterY=0 CenterZ=0 NormalX=0 NormalY=0 NormalZ=1 AngleXU=0 Radius=2.75
  constraints (2):
    c: Coincident(g0,g-1)
    c: Diameter(g0) = 5.5
FEATURE [PartDesign::Pad] Pad020  label="tete002"
  AllowMultiFace = false
  Direction = (1,1,1)
  Length = 3
  Length2 = 100
  Profile = -> Sketch041
  Type = 0
FEATURE [Sketcher::SketchObject] Sketch042
  FullyConstrained = false
  MapMode = 5
  Placement = pos=(0,0,0) rot=(1,0,0;3.14159rad)
  Support = -> [Pad020]
  sketch-geometry (1):
    g0: Circle CenterX=0 CenterY=0 CenterZ=0 NormalX=0 NormalY=0 NormalZ=1 AngleXU=0 Radius=1.5
  constraints (2):
    c: Coincident(g0,g-1)
    c: Diameter(g0) = 3
FEATURE [PartDesign::Pad] Pad021  label="corps002"
  AllowMultiFace = false
  BaseFeature = -> Pad020
  Direction = (1,1,1)
  Length = 6
  Length2 = 100
  Profile = -> Sketch042
  Type = 0
FEATURE [PartDesign::Plane] DatumPlane016
  AttachmentOffset = pos=(0,0,3) rot=(0,0,1;0rad)
  Length = 60
  MapMode = 5
  Placement = pos=(0,0,3) rot=(0,0,1;0rad)
  ResizeMode = 0
  Support = -> [XY_Plane044]
  Width = 60
FEATURE [Sketcher::SketchObject] Sketch043  label="Sketch002"
  FullyConstrained = false
  MapMode = 5
  Placement = pos=(0,0,3) rot=(0,0,1;0rad)
  Support = -> [DatumPlane016]
  sketch-geometry (7):
    g0: LineSegment StartX=0.721688 StartY=-1.25 StartZ=0 EndX=1.44338 EndY=1.0119e-12 EndZ=0
    g1: LineSegment StartX=1.44338 StartY=1.0119e-12 StartZ=0 EndX=0.721688 EndY=1.25 EndZ=0
    g2: LineSegment StartX=0.721688 StartY=1.25 StartZ=0 EndX=-0.721688 EndY=1.25 EndZ=0
    g3: LineSegment StartX=-0.721688 StartY=1.25 StartZ=0 EndX=-1.44338 EndY=8.689e-13 EndZ=0
    g4: LineSegment StartX=-1.44338 StartY=8.689e-13 StartZ=0 EndX=-0.721688 EndY=-1.25 EndZ=0
    g5: LineSegment StartX=-0.721688 StartY=-1.25 StartZ=0 EndX=0.721688 EndY=-1.25 EndZ=0
    g6: Circle CenterX=0 CenterY=0 CenterZ=0 NormalX=0 NormalY=0 NormalZ=1 AngleXU=0 Radius=1.44338
  constraints (16):
    c: Coincident(g0,g1)
    c: Coincident(g1,g2)
    c: Coincident(g2,g3)
    c: Coincident(g3,g4)
    c: Coincident(g4,g5)
    c: Coincident(g5,g0)
    c: Equal(g0, g1-g5) x5
    c: PointOnObject(g0,g6)
    c: PointOnObject(g1,g6)
    c: PointOnObject(g2,g6)
    c: PointOnObject(g3,g6)
    c: PointOnObject(g4,g6)
    c: PointOnObject(g5,g6)
    c: Coincident(g6,g-1)
    c: Horizontal(g2)
    c: DistanceY(g0,g1) = 2.5
FEATURE [PartDesign::Pocket] Pocket020  label="emprunte002"
  AllowMultiFace = false
  BaseFeature = -> Pad021
  Direction = (1,1,1)
  Length = 4
  Length2 = 100
  Profile = -> Sketch043
  Type = 0
FEATURE [PartDesign::Body] Body011  label="visTHCM3x6_DCDC001"
  Group = -> [Sketch041,Pad020,Sketch042,Pad021,DatumPlane016,Sketch043,Pocket020]
  Origin = -> Origin046
  Placement = pos=(-40.02,-40.03,10.89) rot=(0,0,1;0rad)
  Tip = -> Pocket020
FEATURE [Sketcher::SketchObject] Sketch046
  FullyConstrained = false
  MapMode = 5
  Support = -> [XY_Plane045]
  sketch-geometry (1):
    g0: Circle CenterX=0 CenterY=0 CenterZ=0 NormalX=0 NormalY=0 NormalZ=1 AngleXU=0 Radius=2.75
  constraints (2):
    c: Coincident(g0,g-1)
    c: Diameter(g0) = 5.5
FEATURE [PartDesign::Pad] Pad023  label="tete003"
  AllowMultiFace = false
  Direction = (1,1,1)
  Length = 3
  Length2 = 100
  Profile = -> Sketch046
  Type = 0
FEATURE [Sketcher::SketchObject] Sketch044
  FullyConstrained = false
  MapMode = 5
  Placement = pos=(0,0,0) rot=(1,0,0;3.14159rad)
  Support = -> [Pad023]
  sketch-geometry (1):
    g0: Circle CenterX=0 CenterY=0 CenterZ=0 NormalX=0 NormalY=0 NormalZ=1 AngleXU=0 Radius=1.5
  constraints (2):
    c: Coincident(g0,g-1)
    c: Diameter(g0) = 3
FEATURE [PartDesign::Pad] Pad022  label="corps003"
  AllowMultiFace = false
  BaseFeature = -> Pad023
  Direction = (1,1,1)
  Length = 6
  Length2 = 100
  Profile = -> Sketch044
  Type = 0
FEATURE [PartDesign::Plane] DatumPlane017
  AttachmentOffset = pos=(0,0,3) rot=(0,0,1;0rad)
  Length = 60
  MapMode = 5
  Placement = pos=(0,0,3) rot=(0,0,1;0rad)
  ResizeMode = 0
  Support = -> [XY_Plane045]
  Width = 60
FEATURE [Sketcher::SketchObject] Sketch045
  FullyConstrained = false
  MapMode = 5
  Placement = pos=(0,0,3) rot=(0,0,1;0rad)
  Support = -> [DatumPlane017]
  sketch-geometry (7):
    g0: LineSegment StartX=0.721688 StartY=-1.25 StartZ=0 EndX=1.44338 EndY=1.0119e-12 EndZ=0
    g1: LineSegment StartX=1.44338 StartY=1.0119e-12 StartZ=0 EndX=0.721688 EndY=1.25 EndZ=0
    g2: LineSegment StartX=0.721688 StartY=1.25 StartZ=0 EndX=-0.721688 EndY=1.25 EndZ=0
    g3: LineSegment StartX=-0.721688 StartY=1.25 StartZ=0 EndX=-1.44338 EndY=8.689e-13 EndZ=0
    g4: LineSegment StartX=-1.44338 StartY=8.689e-13 StartZ=0 EndX=-0.721688 EndY=-1.25 EndZ=0
    g5: LineSegment StartX=-0.721688 StartY=-1.25 StartZ=0 EndX=0.721688 EndY=-1.25 EndZ=0
    g6: Circle CenterX=0 CenterY=0 CenterZ=0 NormalX=0 NormalY=0 NormalZ=1 AngleXU=0 Radius=1.44338
  constraints (16):
    c: Coincident(g0,g1)
    c: Coincident(g1,g2)
    c: Coincident(g2,g3)
    c: Coincident(g3,g4)
    c: Coincident(g4,g5)
    c: Coincident(g5,g0)
    c: Equal(g0, g1-g5) x5
    c: PointOnObject(g0,g6)
    c: PointOnObject(g1,g6)
    c: PointOnObject(g2,g6)
    c: PointOnObject(g3,g6)
    c: PointOnObject(g4,g6)
    c: PointOnObject(g5,g6)
    c: Coincident(g6,g-1)
    c: Horizontal(g2)
    c: DistanceY(g0,g1) = 2.5
FEATURE [PartDesign::Pocket] Pocket021  label="emprunte003"
  AllowMultiFace = false
  BaseFeature = -> Pad022
  Direction = (1,1,1)
  Length = 4
  Length2 = 100
  Profile = -> Sketch045
  Type = 0
FEATURE [PartDesign::Body] Body012  label="visTHCM3x6_DCDC002"
  Group = -> [Sketch046,Pad023,Sketch044,Pad022,DatumPlane017,Sketch045,Pocket021]
  Origin = -> Origin047
  Placement = pos=(-71.22,-23.18,10.89) rot=(0,0,1;0rad)
  Tip = -> Pocket021
COMPONENT P18 — geometry summary ("switch"; no construction recipe available for this part):
  bounding box: 38.3 x 33.1 x 13.9 mm
  tessellated surface: 3,536 triangles
  volume: 6127 mm^3 (35% of its bounding box)
PROVENANCE & LICENSES
A FreeCAD (.FCStd) document from a public repository crawl; recipes are the document's own serialized feature recipes (and, for linked parts, companion documents' recipes).
License: as declared in the source repository (recorded in the dataset sidecar).
